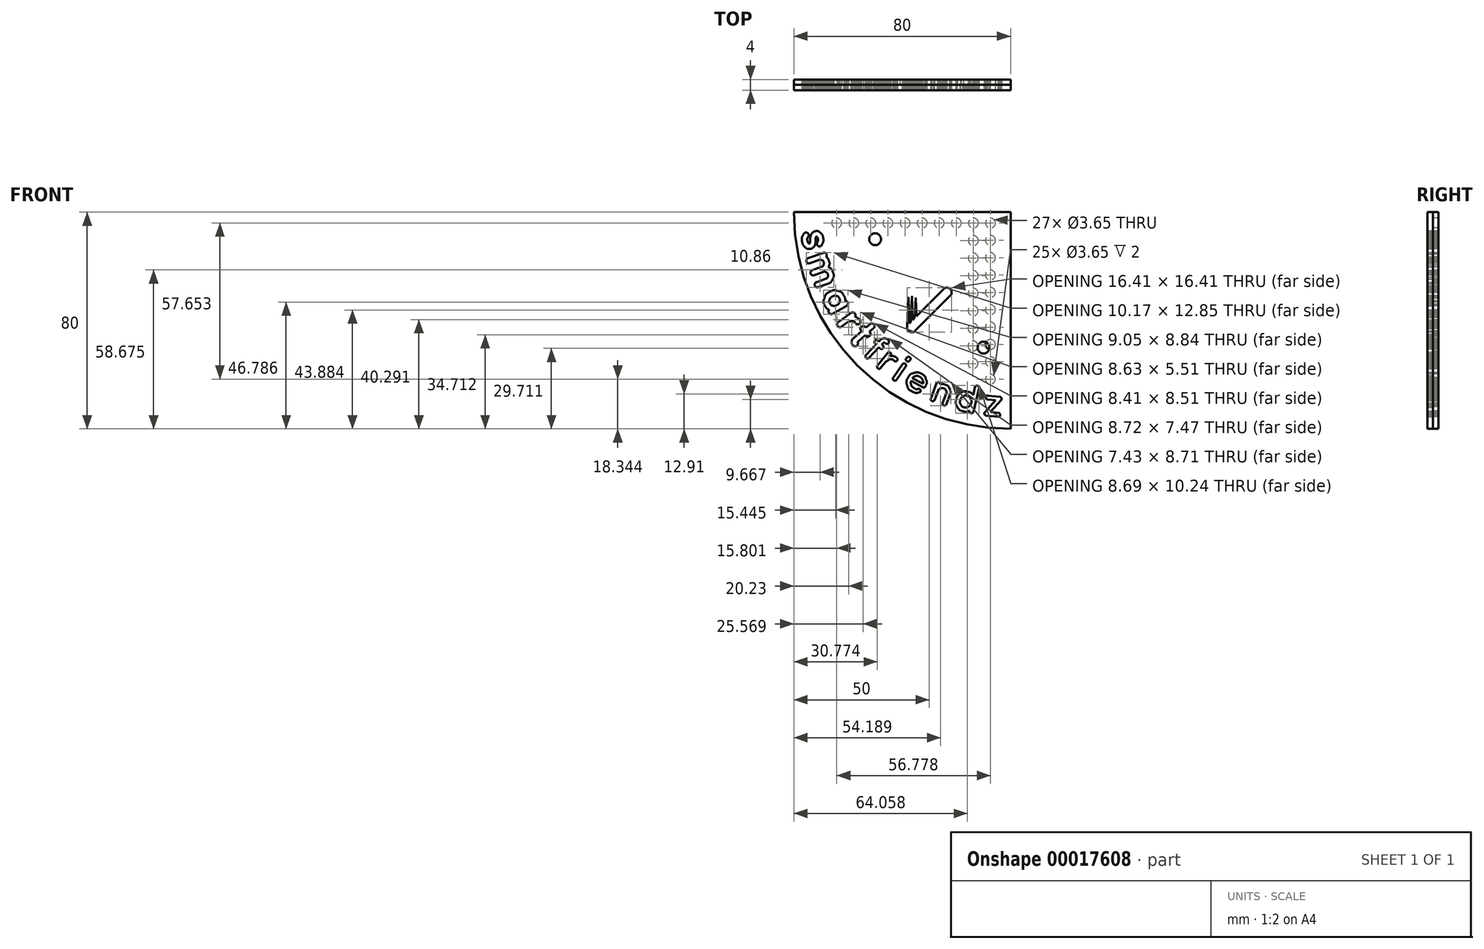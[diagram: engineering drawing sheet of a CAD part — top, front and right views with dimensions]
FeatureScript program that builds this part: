
annotation { "Feature Type Name" : "Feature", "Feature Type Description" : "" }
export const myFeature = defineFeature(function(context is Context, id is Id, definition is map)
    precondition{}
    {
        {
            var Q0;
            Q0=qCreatedBy(makeId("Front.planeOp"),FACE);
            var sketch = newSketch(context, id + "F0", { "sketchPlane" : qUnion([Q0])});
            skFitSpline(sketch, "E0", {"points": [v(17.73, 12.09) * mm, v(17.4, 12.41) * mm, v(16.98, 12.59) * mm, v(16.53, 12.59) * mm]});
            skFitSpline(sketch, "E1", {"points": [v(16.53, 12.59) * mm, v(16.05, 12.59) * mm, v(15.65, 12.41) * mm, v(15.33, 12.09) * mm]});
            skLineSegment(sketch, "E2", {"start": v(15.33, 12.09) * mm, "end": v(5.27, 2.03) * mm});
            skLineSegment(sketch, "E3", {"start": v(5.27, 2.03) * mm, "end": v(5.07, 8.86) * mm});
            skFitSpline(sketch, "E4", {"points": [v(5.07, 8.86) * mm, v(5.04, 8.88) * mm, v(5.02, 8.9) * mm, v(5, 8.93) * mm]});
            skLineSegment(sketch, "E5", {"start": v(5, 8.93) * mm, "end": v(4.72, 1.5) * mm});
            skLineSegment(sketch, "E6", {"start": v(4.72, 1.5) * mm, "end": v(3.94, 0.73) * mm});
            skLineSegment(sketch, "E7", {"start": v(3.94, 0.73) * mm, "end": v(3.67, 9.53) * mm});
            skLineSegment(sketch, "E8", {"start": v(3.67, 9.53) * mm, "end": v(3.64, 9.53) * mm});
            skLineSegment(sketch, "E9", {"start": v(3.64, 9.53) * mm, "end": v(3.32, 0.1) * mm});
            skLineSegment(sketch, "E10", {"start": v(3.32, 0.1) * mm, "end": v(2.64, -0.57) * mm});
            skLineSegment(sketch, "E11", {"start": v(2.64, -0.57) * mm, "end": v(2.37, 9) * mm});
            skFitSpline(sketch, "E12", {"points": [v(2.37, 9) * mm, v(2.35, 9) * mm, v(2.33, 8.97) * mm, v(2.32, 8.93) * mm]});
            skLineSegment(sketch, "E13", {"start": v(2.32, 8.93) * mm, "end": v(1.94, -1.57) * mm});
            skFitSpline(sketch, "E14", {"points": [v(1.94, -1.57) * mm, v(1.9, -1.72) * mm, v(1.87, -1.9) * mm, v(1.87, -2.07) * mm]});
            skFitSpline(sketch, "E15", {"points": [v(1.87, -2.07) * mm, v(1.87, -2.55) * mm, v(2.04, -2.95) * mm, v(2.37, -3.28) * mm]});
            skFitSpline(sketch, "E16", {"points": [v(2.37, -3.28) * mm, v(2.7, -3.6) * mm, v(3.12, -3.78) * mm, v(3.6, -3.8) * mm]});
            skFitSpline(sketch, "E17", {"points": [v(3.6, -3.8) * mm, v(4.07, -3.8) * mm, v(4.47, -3.65) * mm, v(4.82, -3.3) * mm]});
            skLineSegment(sketch, "E18", {"start": v(4.82, -3.3) * mm, "end": v(17.75, 9.63) * mm});
            skFitSpline(sketch, "E19", {"points": [v(17.75, 9.63) * mm, v(18.08, 9.98) * mm, v(18.25, 10.38) * mm, v(18.25, 10.86) * mm]});
            skFitSpline(sketch, "E20", {"points": [v(18.25, 10.86) * mm, v(18.23, 11.34) * mm, v(18.08, 11.76) * mm, v(17.73, 12.09) * mm]});
            skFitSpline(sketch, "E21", {"points": [v(9.35, 19.77) * mm, v(9.35, 20.24) * mm, v(9.17, 20.64) * mm, v(8.82, 21) * mm]});
            skFitSpline(sketch, "E22", {"points": [v(8.82, 21) * mm, v(8.5, 21.32) * mm, v(8.07, 21.5) * mm, v(7.62, 21.5) * mm]});
            skFitSpline(sketch, "E23", {"points": [v(7.62, 21.5) * mm, v(7.45, 21.5) * mm, v(7.3, 21.47) * mm, v(7.15, 21.42) * mm]});
            skLineSegment(sketch, "E24", {"start": v(7.15, 21.42) * mm, "end": v(-3.41, 21.1) * mm});
            skFitSpline(sketch, "E25", {"points": [v(-3.41, 21.1) * mm, v(-3.44, 21.07) * mm, v(-3.46, 21.07) * mm, v(-3.46, 21.04) * mm]});
            skLineSegment(sketch, "E26", {"start": v(-3.46, 21.04) * mm, "end": v(6.15, 20.7) * mm});
            skLineSegment(sketch, "E27", {"start": v(6.15, 20.7) * mm, "end": v(5.47, 20.02) * mm});
            skLineSegment(sketch, "E28", {"start": v(5.47, 20.02) * mm, "end": v(-4.09, 19.74) * mm});
            skLineSegment(sketch, "E29", {"start": v(-4.09, 19.74) * mm, "end": v(4.84, 19.42) * mm});
            skLineSegment(sketch, "E30", {"start": v(4.84, 19.42) * mm, "end": v(4.07, 18.64) * mm});
            skLineSegment(sketch, "E31", {"start": v(4.07, 18.64) * mm, "end": v(-3.56, 18.42) * mm});
            skFitSpline(sketch, "E32", {"points": [v(-3.56, 18.42) * mm, v(-3.54, 18.4) * mm, v(-3.54, 18.4) * mm, v(-3.51, 18.37) * mm]});
            skLineSegment(sketch, "E33", {"start": v(-3.51, 18.37) * mm, "end": v(3.57, 18.11) * mm});
            skLineSegment(sketch, "E34", {"start": v(3.57, 18.11) * mm, "end": v(-6.54, 8.06) * mm});
            skFitSpline(sketch, "E35", {"points": [v(-6.54, 8.06) * mm, v(-6.86, 7.73) * mm, v(-7.04, 7.3) * mm, v(-7.04, 6.86) * mm]});
            skFitSpline(sketch, "E36", {"points": [v(-7.04, 6.86) * mm, v(-7.04, 6.38) * mm, v(-6.86, 5.98) * mm, v(-6.54, 5.66) * mm]});
            skFitSpline(sketch, "E37", {"points": [v(-6.54, 5.66) * mm, v(-6.21, 5.33) * mm, v(-5.79, 5.16) * mm, v(-5.31, 5.13) * mm]});
            skFitSpline(sketch, "E38", {"points": [v(-5.31, 5.13) * mm, v(-4.84, 5.13) * mm, v(-4.44, 5.28) * mm, v(-4.09, 5.63) * mm]});
            skLineSegment(sketch, "E39", {"start": v(-4.09, 5.63) * mm, "end": v(8.85, 18.57) * mm});
            skFitSpline(sketch, "E40", {"points": [v(8.85, 18.57) * mm, v(9.2, 18.9) * mm, v(9.35, 19.3) * mm, v(9.35, 19.77) * mm]});
            skFitSpline(sketch, "E41", {"points": [v(-33.8, 26.97) * mm, v(-33.43, 27.05) * mm, v(-33.08, 27.22) * mm, v(-32.76, 27.52) * mm]});
            skFitSpline(sketch, "E42", {"points": [v(-32.76, 27.52) * mm, v(-32.43, 27.82) * mm, v(-32.18, 28.22) * mm, v(-32.06, 28.72) * mm]});
            skFitSpline(sketch, "E43", {"points": [v(-32.06, 28.72) * mm, v(-31.93, 29.2) * mm, v(-31.88, 29.7) * mm, v(-31.88, 30.25) * mm]});
            skLineSegment(sketch, "E44", {"start": v(-31.88, 30.25) * mm, "end": v(-31.88, 30.27) * mm});
            skLineSegment(sketch, "E45", {"start": v(-31.88, 30.27) * mm, "end": v(-31.88, 30.32) * mm});
            skFitSpline(sketch, "E46", {"points": [v(-31.88, 30.32) * mm, v(-31.88, 30.82) * mm, v(-31.83, 31.17) * mm, v(-31.73, 31.4) * mm]});
            skFitSpline(sketch, "E47", {"points": [v(-31.73, 31.4) * mm, v(-31.72, 31.45) * mm, v(-31.7, 31.48) * mm, v(-31.68, 31.5) * mm]});
            skFitSpline(sketch, "E48", {"points": [v(-31.68, 31.5) * mm, v(-31.66, 31.52) * mm, v(-31.64, 31.52) * mm, v(-31.6, 31.52) * mm]});
            skFitSpline(sketch, "E49", {"points": [v(-31.6, 31.52) * mm, v(-31.57, 31.52) * mm, v(-31.51, 31.47) * mm, v(-31.43, 31.37) * mm]});
            skFitSpline(sketch, "E50", {"points": [v(-31.43, 31.37) * mm, v(-31.26, 31.2) * mm, v(-31.13, 30.97) * mm, v(-31.06, 30.65) * mm]});
            skFitSpline(sketch, "E51", {"points": [v(-31.06, 30.65) * mm, v(-31, 30.32) * mm, v(-31.08, 29.87) * mm, v(-31.33, 29.3) * mm]});
            skFitSpline(sketch, "E52", {"points": [v(-31.33, 29.3) * mm, v(-31.46, 29.05) * mm, v(-31.46, 28.77) * mm, v(-31.36, 28.52) * mm]});
            skFitSpline(sketch, "E53", {"points": [v(-31.36, 28.52) * mm, v(-31.26, 28.27) * mm, v(-31.08, 28.1) * mm, v(-30.83, 27.97) * mm]});
            skFitSpline(sketch, "E54", {"points": [v(-30.83, 27.97) * mm, v(-30.58, 27.87) * mm, v(-30.33, 27.9) * mm, v(-30.08, 28) * mm]});
            skFitSpline(sketch, "E55", {"points": [v(-30.08, 28) * mm, v(-29.83, 28.1) * mm, v(-29.66, 28.27) * mm, v(-29.56, 28.52) * mm]});
            skFitSpline(sketch, "E56", {"points": [v(-29.56, 28.52) * mm, v(-29.15, 29.45) * mm, v(-29, 30.27) * mm, v(-29.13, 31) * mm]});
            skFitSpline(sketch, "E57", {"points": [v(-29.13, 31) * mm, v(-29.25, 31.72) * mm, v(-29.58, 32.33) * mm, v(-30.08, 32.83) * mm]});
            skFitSpline(sketch, "E58", {"points": [v(-30.08, 32.83) * mm, v(-30.68, 33.35) * mm, v(-31.33, 33.58) * mm, v(-32.03, 33.45) * mm]});
            skFitSpline(sketch, "E59", {"points": [v(-32.03, 33.45) * mm, v(-32.4, 33.38) * mm, v(-32.73, 33.23) * mm, v(-33, 32.98) * mm]});
            skFitSpline(sketch, "E60", {"points": [v(-33, 32.98) * mm, v(-33.33, 32.65) * mm, v(-33.58, 32.25) * mm, v(-33.7, 31.8) * mm]});
            skFitSpline(sketch, "E61", {"points": [v(-33.7, 31.8) * mm, v(-33.83, 31.35) * mm, v(-33.88, 30.85) * mm, v(-33.88, 30.3) * mm]});
            skLineSegment(sketch, "E62", {"start": v(-33.88, 30.3) * mm, "end": v(-33.88, 30.27) * mm});
            skFitSpline(sketch, "E63", {"points": [v(-33.88, 30.27) * mm, v(-33.88, 29.75) * mm, v(-33.96, 29.35) * mm, v(-34.06, 29.1) * mm]});
            skFitSpline(sketch, "E64", {"points": [v(-34.06, 29.1) * mm, v(-34.1, 29.03) * mm, v(-34.12, 28.99) * mm, v(-34.13, 28.97) * mm]});
            skLineSegment(sketch, "E65", {"start": v(-34.13, 28.97) * mm, "end": v(-34.16, 28.95) * mm});
            skFitSpline(sketch, "E66", {"points": [v(-34.16, 28.95) * mm, v(-34.18, 28.93) * mm, v(-34.2, 28.92) * mm, v(-34.26, 28.92) * mm]});
            skFitSpline(sketch, "E67", {"points": [v(-34.26, 28.92) * mm, v(-34.3, 28.92) * mm, v(-34.4, 28.97) * mm, v(-34.5, 29.07) * mm]});
            skFitSpline(sketch, "E68", {"points": [v(-34.5, 29.07) * mm, v(-34.73, 29.3) * mm, v(-34.86, 29.6) * mm, v(-34.93, 29.92) * mm]});
            skFitSpline(sketch, "E69", {"points": [v(-34.93, 29.92) * mm, v(-35.03, 30.42) * mm, v(-34.93, 30.97) * mm, v(-34.6, 31.52) * mm]});
            skFitSpline(sketch, "E70", {"points": [v(-34.6, 31.52) * mm, v(-34.48, 31.75) * mm, v(-34.43, 32) * mm, v(-34.5, 32.28) * mm]});
            skFitSpline(sketch, "E71", {"points": [v(-34.5, 32.28) * mm, v(-34.58, 32.55) * mm, v(-34.76, 32.75) * mm, v(-34.98, 32.85) * mm]});
            skFitSpline(sketch, "E72", {"points": [v(-34.98, 32.85) * mm, v(-35.2, 32.98) * mm, v(-35.46, 33.03) * mm, v(-35.73, 32.93) * mm]});
            skFitSpline(sketch, "E73", {"points": [v(-35.73, 32.93) * mm, v(-36, 32.85) * mm, v(-36.18, 32.7) * mm, v(-36.3, 32.48) * mm]});
            skFitSpline(sketch, "E74", {"points": [v(-36.3, 32.48) * mm, v(-36.84, 31.47) * mm, v(-37.04, 30.5) * mm, v(-36.86, 29.55) * mm]});
            skFitSpline(sketch, "E75", {"points": [v(-36.86, 29.55) * mm, v(-36.71, 28.8) * mm, v(-36.39, 28.17) * mm, v(-35.86, 27.65) * mm]});
            skFitSpline(sketch, "E76", {"points": [v(-35.86, 27.65) * mm, v(-35.36, 27.17) * mm, v(-34.83, 26.95) * mm, v(-34.23, 26.95) * mm]});
            skFitSpline(sketch, "E77", {"points": [v(-34.23, 26.95) * mm, v(-34.08, 26.92) * mm, v(-33.93, 26.95) * mm, v(-33.8, 26.97) * mm]});
            skFitSpline(sketch, "E78", {"points": [v(-25.65, 15.74) * mm, v(-25.25, 16.56) * mm, v(-25.23, 17.44) * mm, v(-25.55, 18.37) * mm]});
            skFitSpline(sketch, "E79", {"points": [v(-25.55, 18.37) * mm, v(-25.85, 19.22) * mm, v(-26.4, 19.82) * mm, v(-27.2, 20.2) * mm]});
            skFitSpline(sketch, "E80", {"points": [v(-27.2, 20.2) * mm, v(-26.83, 21) * mm, v(-26.78, 21.84) * mm, v(-27.1, 22.72) * mm]});
            skFitSpline(sketch, "E81", {"points": [v(-27.1, 22.72) * mm, v(-27.28, 23.22) * mm, v(-27.58, 23.67) * mm, v(-27.98, 24.04) * mm]});
            skFitSpline(sketch, "E82", {"points": [v(-27.98, 24.04) * mm, v(-27.8, 24.3) * mm, v(-27.78, 24.6) * mm, v(-27.88, 24.92) * mm]});
            skFitSpline(sketch, "E83", {"points": [v(-27.88, 24.92) * mm, v(-27.98, 25.17) * mm, v(-28.13, 25.37) * mm, v(-28.38, 25.47) * mm]});
            skFitSpline(sketch, "E84", {"points": [v(-28.38, 25.47) * mm, v(-28.63, 25.6) * mm, v(-28.88, 25.6) * mm, v(-29.15, 25.5) * mm]});
            skLineSegment(sketch, "E85", {"start": v(-29.15, 25.5) * mm, "end": v(-34.7, 23.52) * mm});
            skFitSpline(sketch, "E86", {"points": [v(-34.7, 23.52) * mm, v(-34.93, 23.44) * mm, v(-35.1, 23.3) * mm, v(-35.2, 23.1) * mm]});
            skFitSpline(sketch, "E87", {"points": [v(-35.2, 23.1) * mm, v(-35.3, 22.9) * mm, v(-35.36, 22.7) * mm, v(-35.33, 22.44) * mm]});
            skLineSegment(sketch, "E88", {"start": v(-35.33, 22.44) * mm, "end": v(-35.28, 22.27) * mm});
            skLineSegment(sketch, "E89", {"start": v(-35.28, 22.27) * mm, "end": v(-35.28, 22.24) * mm});
            skFitSpline(sketch, "E90", {"points": [v(-35.28, 22.24) * mm, v(-35.16, 21.87) * mm, v(-34.86, 21.62) * mm, v(-34.43, 21.57) * mm]});
            skLineSegment(sketch, "E91", {"start": v(-34.43, 21.57) * mm, "end": v(-34.38, 21.57) * mm});
            skLineSegment(sketch, "E92", {"start": v(-34.38, 21.57) * mm, "end": v(-34.3, 21.6) * mm});
            skLineSegment(sketch, "E93", {"start": v(-34.3, 21.6) * mm, "end": v(-34.2, 21.6) * mm});
            skLineSegment(sketch, "E94", {"start": v(-34.2, 21.6) * mm, "end": v(-34.06, 21.64) * mm});
            skLineSegment(sketch, "E95", {"start": v(-34.06, 21.64) * mm, "end": v(-30.68, 22.84) * mm});
            skFitSpline(sketch, "E96", {"points": [v(-30.68, 22.84) * mm, v(-30.33, 22.97) * mm, v(-29.98, 22.94) * mm, v(-29.63, 22.8) * mm]});
            skFitSpline(sketch, "E97", {"points": [v(-29.63, 22.8) * mm, v(-29.28, 22.64) * mm, v(-29.05, 22.4) * mm, v(-28.95, 22.04) * mm]});
            skFitSpline(sketch, "E98", {"points": [v(-28.95, 22.04) * mm, v(-28.83, 21.7) * mm, v(-28.85, 21.37) * mm, v(-29, 21.02) * mm]});
            skFitSpline(sketch, "E99", {"points": [v(-29, 21.02) * mm, v(-29.15, 20.67) * mm, v(-29.4, 20.44) * mm, v(-29.73, 20.32) * mm]});
            skLineSegment(sketch, "E100", {"start": v(-29.73, 20.32) * mm, "end": v(-33.13, 19.12) * mm});
            skFitSpline(sketch, "E101", {"points": [v(-33.13, 19.12) * mm, v(-33.38, 19.04) * mm, v(-33.56, 18.87) * mm, v(-33.68, 18.6) * mm]});
            skFitSpline(sketch, "E102", {"points": [v(-33.68, 18.6) * mm, v(-33.8, 18.34) * mm, v(-33.8, 18.09) * mm, v(-33.73, 17.84) * mm]});
            skFitSpline(sketch, "E103", {"points": [v(-33.73, 17.84) * mm, v(-33.63, 17.59) * mm, v(-33.48, 17.41) * mm, v(-33.23, 17.29) * mm]});
            skFitSpline(sketch, "E104", {"points": [v(-33.23, 17.29) * mm, v(-32.98, 17.16) * mm, v(-32.73, 17.16) * mm, v(-32.48, 17.24) * mm]});
            skLineSegment(sketch, "E105", {"start": v(-32.48, 17.24) * mm, "end": v(-29.1, 18.44) * mm});
            skFitSpline(sketch, "E106", {"points": [v(-29.1, 18.44) * mm, v(-28.75, 18.54) * mm, v(-28.4, 18.52) * mm, v(-28.08, 18.37) * mm]});
            skFitSpline(sketch, "E107", {"points": [v(-28.08, 18.37) * mm, v(-27.75, 18.2) * mm, v(-27.53, 17.94) * mm, v(-27.4, 17.61) * mm]});
            skFitSpline(sketch, "E108", {"points": [v(-27.4, 17.61) * mm, v(-27.28, 17.26) * mm, v(-27.3, 16.94) * mm, v(-27.45, 16.59) * mm]});
            skFitSpline(sketch, "E109", {"points": [v(-27.45, 16.59) * mm, v(-27.6, 16.24) * mm, v(-27.88, 16.01) * mm, v(-28.23, 15.89) * mm]});
            skLineSegment(sketch, "E110", {"start": v(-28.23, 15.89) * mm, "end": v(-31.58, 14.69) * mm});
            skFitSpline(sketch, "E111", {"points": [v(-31.58, 14.69) * mm, v(-31.83, 14.59) * mm, v(-32.03, 14.41) * mm, v(-32.13, 14.16) * mm]});
            skFitSpline(sketch, "E112", {"points": [v(-32.13, 14.16) * mm, v(-32.26, 13.91) * mm, v(-32.26, 13.66) * mm, v(-32.16, 13.41) * mm]});
            skFitSpline(sketch, "E113", {"points": [v(-32.16, 13.41) * mm, v(-32.06, 13.16) * mm, v(-31.9, 12.96) * mm, v(-31.66, 12.86) * mm]});
            skFitSpline(sketch, "E114", {"points": [v(-31.66, 12.86) * mm, v(-31.53, 12.79) * mm, v(-31.38, 12.76) * mm, v(-31.23, 12.76) * mm]});
            skFitSpline(sketch, "E115", {"points": [v(-31.23, 12.76) * mm, v(-31.13, 12.76) * mm, v(-31, 12.79) * mm, v(-30.9, 12.81) * mm]});
            skLineSegment(sketch, "E116", {"start": v(-30.9, 12.81) * mm, "end": v(-27.55, 14.01) * mm});
            skFitSpline(sketch, "E117", {"points": [v(-27.55, 14.01) * mm, v(-26.68, 14.34) * mm, v(-26.05, 14.91) * mm, v(-25.65, 15.74) * mm]});
            skFitSpline(sketch, "E118", {"points": [v(-20.05, 6.53) * mm, v(-19.97, 6.8) * mm, v(-20, 7.03) * mm, v(-20.12, 7.26) * mm]});
            skFitSpline(sketch, "E119", {"points": [v(-20.12, 7.26) * mm, v(-20.25, 7.48) * mm, v(-20.42, 7.63) * mm, v(-20.65, 7.7) * mm]});
            skFitSpline(sketch, "E120", {"points": [v(-20.65, 7.7) * mm, v(-20.77, 7.76) * mm, v(-20.92, 7.78) * mm, v(-21.05, 7.76) * mm]});
            skFitSpline(sketch, "E121", {"points": [v(-21.05, 7.76) * mm, v(-21.02, 8.46) * mm, v(-21.15, 9.1) * mm, v(-21.5, 9.68) * mm]});
            skFitSpline(sketch, "E122", {"points": [v(-21.5, 9.68) * mm, v(-22.02, 10.6) * mm, v(-22.8, 11.21) * mm, v(-23.83, 11.46) * mm]});
            skFitSpline(sketch, "E123", {"points": [v(-23.83, 11.46) * mm, v(-24.85, 11.71) * mm, v(-25.85, 11.56) * mm, v(-26.78, 11.03) * mm]});
            skFitSpline(sketch, "E124", {"points": [v(-26.78, 11.03) * mm, v(-27.73, 10.5) * mm, v(-28.35, 9.73) * mm, v(-28.68, 8.73) * mm]});
            skFitSpline(sketch, "E125", {"points": [v(-28.68, 8.73) * mm, v(-29, 7.73) * mm, v(-28.9, 6.76) * mm, v(-28.38, 5.83) * mm]});
            skFitSpline(sketch, "E126", {"points": [v(-28.38, 5.83) * mm, v(-28.05, 5.23) * mm, v(-27.58, 4.78) * mm, v(-26.98, 4.43) * mm]});
            skFitSpline(sketch, "E127", {"points": [v(-26.98, 4.43) * mm, v(-27.05, 4.3) * mm, v(-27.1, 4.18) * mm, v(-27.13, 4.05) * mm]});
            skFitSpline(sketch, "E128", {"points": [v(-27.13, 4.05) * mm, v(-27.18, 3.83) * mm, v(-27.13, 3.6) * mm, v(-27, 3.38) * mm]});
            skFitSpline(sketch, "E129", {"points": [v(-27, 3.38) * mm, v(-26.88, 3.15) * mm, v(-26.68, 3) * mm, v(-26.43, 2.93) * mm]});
            skFitSpline(sketch, "E130", {"points": [v(-26.43, 2.93) * mm, v(-26.33, 2.9) * mm, v(-26.25, 2.88) * mm, v(-26.15, 2.88) * mm]});
            skFitSpline(sketch, "E131", {"points": [v(-26.15, 2.88) * mm, v(-26, 2.88) * mm, v(-25.83, 2.93) * mm, v(-25.68, 3) * mm]});
            skLineSegment(sketch, "E132", {"start": v(-25.68, 3) * mm, "end": v(-20.52, 5.88) * mm});
            skFitSpline(sketch, "E133", {"points": [v(-20.52, 5.88) * mm, v(-20.27, 6.08) * mm, v(-20.12, 6.28) * mm, v(-20.05, 6.53) * mm]});
            skFitSpline(sketch, "E134", {"points": [v(-23.1, 7.36) * mm, v(-23.28, 6.86) * mm, v(-23.58, 6.48) * mm, v(-24.08, 6.2) * mm]});
            skFitSpline(sketch, "E135", {"points": [v(-24.08, 6.2) * mm, v(-24.55, 5.93) * mm, v(-25.05, 5.86) * mm, v(-25.53, 5.98) * mm]});
            skFitSpline(sketch, "E136", {"points": [v(-25.53, 5.98) * mm, v(-26.03, 6.1) * mm, v(-26.38, 6.38) * mm, v(-26.63, 6.83) * mm]});
            skFitSpline(sketch, "E137", {"points": [v(-26.63, 6.83) * mm, v(-26.88, 7.28) * mm, v(-26.93, 7.73) * mm, v(-26.75, 8.2) * mm]});
            skFitSpline(sketch, "E138", {"points": [v(-26.75, 8.2) * mm, v(-26.58, 8.68) * mm, v(-26.28, 9.06) * mm, v(-25.78, 9.33) * mm]});
            skFitSpline(sketch, "E139", {"points": [v(-25.78, 9.33) * mm, v(-25.43, 9.53) * mm, v(-25.08, 9.63) * mm, v(-24.73, 9.63) * mm]});
            skFitSpline(sketch, "E140", {"points": [v(-24.73, 9.63) * mm, v(-24.58, 9.63) * mm, v(-24.43, 9.6) * mm, v(-24.3, 9.58) * mm]});
            skFitSpline(sketch, "E141", {"points": [v(-24.3, 9.58) * mm, v(-23.8, 9.48) * mm, v(-23.45, 9.2) * mm, v(-23.2, 8.76) * mm]});
            skFitSpline(sketch, "E142", {"points": [v(-23.2, 8.76) * mm, v(-22.98, 8.3) * mm, v(-22.93, 7.86) * mm, v(-23.1, 7.36) * mm]});
            skFitSpline(sketch, "E143", {"points": [v(-17.2, -0.47) * mm, v(-17.05, -0.7) * mm, v(-16.82, -0.82) * mm, v(-16.55, -0.87) * mm]});
            skFitSpline(sketch, "E144", {"points": [v(-16.55, -0.87) * mm, v(-16.27, -0.92) * mm, v(-16.02, -0.85) * mm, v(-15.82, -0.7) * mm]});
            skFitSpline(sketch, "E145", {"points": [v(-15.82, -0.7) * mm, v(-15.6, -0.55) * mm, v(-15.47, -0.32) * mm, v(-15.45, -0.07) * mm]});
            skFitSpline(sketch, "E146", {"points": [v(-15.45, -0.07) * mm, v(-15.4, 0.18) * mm, v(-15.5, 0.48) * mm, v(-15.72, 0.78) * mm]});
            skFitSpline(sketch, "E147", {"points": [v(-15.72, 0.78) * mm, v(-15.92, 1.08) * mm, v(-16.22, 1.33) * mm, v(-16.62, 1.58) * mm]});
            skFitSpline(sketch, "E148", {"points": [v(-16.62, 1.58) * mm, v(-16.87, 1.73) * mm, v(-17.15, 1.85) * mm, v(-17.4, 1.93) * mm]});
            skFitSpline(sketch, "E149", {"points": [v(-17.4, 1.93) * mm, v(-17.3, 2.05) * mm, v(-17.25, 2.2) * mm, v(-17.22, 2.38) * mm]});
            skFitSpline(sketch, "E150", {"points": [v(-17.22, 2.38) * mm, v(-17.2, 2.65) * mm, v(-17.25, 2.88) * mm, v(-17.42, 3.1) * mm]});
            skFitSpline(sketch, "E151", {"points": [v(-17.42, 3.1) * mm, v(-17.57, 3.33) * mm, v(-17.8, 3.45) * mm, v(-18.05, 3.5) * mm]});
            skFitSpline(sketch, "E152", {"points": [v(-18.05, 3.5) * mm, v(-18.32, 3.55) * mm, v(-18.55, 3.5) * mm, v(-18.77, 3.33) * mm]});
            skLineSegment(sketch, "E153", {"start": v(-18.77, 3.33) * mm, "end": v(-23.58, -0.12) * mm});
            skFitSpline(sketch, "E154", {"points": [v(-23.58, -0.12) * mm, v(-23.8, -0.27) * mm, v(-23.93, -0.5) * mm, v(-23.98, -0.77) * mm]});
            skFitSpline(sketch, "E155", {"points": [v(-23.98, -0.77) * mm, v(-24.03, -1.05) * mm, v(-23.95, -1.3) * mm, v(-23.8, -1.52) * mm]});
            skFitSpline(sketch, "E156", {"points": [v(-23.8, -1.52) * mm, v(-23.65, -1.75) * mm, v(-23.43, -1.87) * mm, v(-23.15, -1.92) * mm]});
            skFitSpline(sketch, "E157", {"points": [v(-23.15, -1.92) * mm, v(-23.1, -1.92) * mm, v(-23.03, -1.95) * mm, v(-22.98, -1.95) * mm]});
            skFitSpline(sketch, "E158", {"points": [v(-22.98, -1.95) * mm, v(-22.78, -1.95) * mm, v(-22.6, -1.9) * mm, v(-22.43, -1.77) * mm]});
            skLineSegment(sketch, "E159", {"start": v(-22.43, -1.77) * mm, "end": v(-20.15, -0.12) * mm});
            skFitSpline(sketch, "E160", {"points": [v(-20.15, -0.12) * mm, v(-18.67, 0.33) * mm, v(-17.7, 0.2) * mm, v(-17.2, -0.47) * mm]});
            skFitSpline(sketch, "E161", {"points": [v(-10.2, -1.62) * mm, v(-10.17, -1.35) * mm, v(-10.27, -1.1) * mm, v(-10.44, -0.9) * mm]});
            skFitSpline(sketch, "E162", {"points": [v(-10.44, -0.9) * mm, v(-10.62, -0.7) * mm, v(-10.87, -0.57) * mm, v(-11.14, -0.55) * mm]});
            skFitSpline(sketch, "E163", {"points": [v(-11.14, -0.55) * mm, v(-11.42, -0.52) * mm, v(-11.67, -0.6) * mm, v(-11.9, -0.8) * mm]});
            skLineSegment(sketch, "E164", {"start": v(-11.9, -0.8) * mm, "end": v(-13.4, -2.1) * mm});
            skLineSegment(sketch, "E165", {"start": v(-13.4, -2.1) * mm, "end": v(-13.57, -1.92) * mm});
            skFitSpline(sketch, "E166", {"points": [v(-13.57, -1.92) * mm, v(-13.74, -1.72) * mm, v(-14, -1.6) * mm, v(-14.27, -1.57) * mm]});
            skFitSpline(sketch, "E167", {"points": [v(-14.27, -1.57) * mm, v(-14.54, -1.55) * mm, v(-14.8, -1.65) * mm, v(-15, -1.82) * mm]});
            skFitSpline(sketch, "E168", {"points": [v(-15, -1.82) * mm, v(-15.2, -2) * mm, v(-15.32, -2.25) * mm, v(-15.35, -2.52) * mm]});
            skFitSpline(sketch, "E169", {"points": [v(-15.35, -2.52) * mm, v(-15.37, -2.8) * mm, v(-15.27, -3.05) * mm, v(-15.1, -3.25) * mm]});
            skLineSegment(sketch, "E170", {"start": v(-15.1, -3.25) * mm, "end": v(-14.92, -3.43) * mm});
            skLineSegment(sketch, "E171", {"start": v(-14.92, -3.43) * mm, "end": v(-17.92, -6.05) * mm});
            skFitSpline(sketch, "E172", {"points": [v(-17.92, -6.05) * mm, v(-18.3, -6.38) * mm, v(-18.52, -6.83) * mm, v(-18.55, -7.33) * mm]});
            skFitSpline(sketch, "E173", {"points": [v(-18.55, -7.33) * mm, v(-18.57, -7.83) * mm, v(-18.42, -8.28) * mm, v(-18.1, -8.68) * mm]});
            skFitSpline(sketch, "E174", {"points": [v(-18.1, -8.68) * mm, v(-17.92, -8.88) * mm, v(-17.67, -9) * mm, v(-17.4, -9.03) * mm]});
            skFitSpline(sketch, "E175", {"points": [v(-17.4, -9.03) * mm, v(-17.37, -9.03) * mm, v(-17.35, -9.03) * mm, v(-17.32, -9.03) * mm]});
            skFitSpline(sketch, "E176", {"points": [v(-17.32, -9.03) * mm, v(-17.07, -9.03) * mm, v(-16.85, -8.95) * mm, v(-16.67, -8.78) * mm]});
            skFitSpline(sketch, "E177", {"points": [v(-16.67, -8.78) * mm, v(-16.47, -8.6) * mm, v(-16.35, -8.35) * mm, v(-16.32, -8.08) * mm]});
            skFitSpline(sketch, "E178", {"points": [v(-16.32, -8.08) * mm, v(-16.3, -7.85) * mm, v(-16.35, -7.65) * mm, v(-16.45, -7.48) * mm]});
            skLineSegment(sketch, "E179", {"start": v(-16.45, -7.48) * mm, "end": v(-13.57, -4.95) * mm});
            skLineSegment(sketch, "E180", {"start": v(-13.57, -4.95) * mm, "end": v(-13.44, -5.1) * mm});
            skFitSpline(sketch, "E181", {"points": [v(-13.44, -5.1) * mm, v(-13.27, -5.3) * mm, v(-13.02, -5.43) * mm, v(-12.74, -5.45) * mm]});
            skFitSpline(sketch, "E182", {"points": [v(-12.74, -5.45) * mm, v(-12.47, -5.48) * mm, v(-12.22, -5.38) * mm, v(-12, -5.2) * mm]});
            skFitSpline(sketch, "E183", {"points": [v(-12, -5.2) * mm, v(-11.8, -5.03) * mm, v(-11.67, -4.78) * mm, v(-11.67, -4.5) * mm]});
            skFitSpline(sketch, "E184", {"points": [v(-11.67, -4.5) * mm, v(-11.64, -4.23) * mm, v(-11.74, -3.98) * mm, v(-11.92, -3.78) * mm]});
            skLineSegment(sketch, "E185", {"start": v(-11.92, -3.78) * mm, "end": v(-12.04, -3.63) * mm});
            skLineSegment(sketch, "E186", {"start": v(-12.04, -3.63) * mm, "end": v(-10.54, -2.32) * mm});
            skFitSpline(sketch, "E187", {"points": [v(-10.54, -2.32) * mm, v(-10.32, -2.15) * mm, v(-10.2, -1.9) * mm, v(-10.2, -1.62) * mm]});
            skFitSpline(sketch, "E188", {"points": [v(-4.81, -7.33) * mm, v(-4.81, -7.1) * mm, v(-4.89, -6.93) * mm, v(-5.04, -6.8) * mm]});
            skFitSpline(sketch, "E189", {"points": [v(-5.04, -6.8) * mm, v(-5.56, -6.3) * mm, v(-6.11, -6.05) * mm, v(-6.66, -6.1) * mm]});
            skFitSpline(sketch, "E190", {"points": [v(-6.66, -6.1) * mm, v(-7.21, -6.15) * mm, v(-7.76, -6.45) * mm, v(-8.34, -7.05) * mm]});
            skLineSegment(sketch, "E191", {"start": v(-8.34, -7.05) * mm, "end": v(-8.54, -7.25) * mm});
            skLineSegment(sketch, "E192", {"start": v(-8.54, -7.25) * mm, "end": v(-8.87, -6.93) * mm});
            skFitSpline(sketch, "E193", {"points": [v(-8.87, -6.93) * mm, v(-9.02, -6.78) * mm, v(-9.2, -6.7) * mm, v(-9.42, -6.7) * mm]});
            skFitSpline(sketch, "E194", {"points": [v(-9.42, -6.7) * mm, v(-9.64, -6.7) * mm, v(-9.82, -6.78) * mm, v(-9.97, -6.93) * mm]});
            skFitSpline(sketch, "E195", {"points": [v(-9.97, -6.93) * mm, v(-10.12, -7.08) * mm, v(-10.2, -7.25) * mm, v(-10.17, -7.48) * mm]});
            skFitSpline(sketch, "E196", {"points": [v(-10.17, -7.48) * mm, v(-10.17, -7.7) * mm, v(-10.1, -7.88) * mm, v(-9.92, -8.03) * mm]});
            skLineSegment(sketch, "E197", {"start": v(-9.92, -8.03) * mm, "end": v(-9.6, -8.35) * mm});
            skLineSegment(sketch, "E198", {"start": v(-9.6, -8.35) * mm, "end": v(-9.64, -8.4) * mm});
            skLineSegment(sketch, "E199", {"start": v(-9.64, -8.4) * mm, "end": v(-13.3, -12.2) * mm});
            skFitSpline(sketch, "E200", {"points": [v(-13.3, -12.2) * mm, v(-13.44, -12.36) * mm, v(-13.52, -12.53) * mm, v(-13.52, -12.76) * mm]});
            skFitSpline(sketch, "E201", {"points": [v(-13.52, -12.76) * mm, v(-13.52, -12.96) * mm, v(-13.44, -13.13) * mm, v(-13.3, -13.28) * mm]});
            skFitSpline(sketch, "E202", {"points": [v(-13.3, -13.28) * mm, v(-13.14, -13.43) * mm, v(-12.97, -13.5) * mm, v(-12.74, -13.5) * mm]});
            skFitSpline(sketch, "E203", {"points": [v(-12.74, -13.5) * mm, v(-12.54, -13.5) * mm, v(-12.37, -13.43) * mm, v(-12.22, -13.28) * mm]});
            skLineSegment(sketch, "E204", {"start": v(-12.22, -13.28) * mm, "end": v(-8.52, -9.4) * mm});
            skLineSegment(sketch, "E205", {"start": v(-8.52, -9.4) * mm, "end": v(-8.14, -9.75) * mm});
            skFitSpline(sketch, "E206", {"points": [v(-8.14, -9.75) * mm, v(-7.99, -9.9) * mm, v(-7.81, -9.98) * mm, v(-7.59, -9.95) * mm]});
            skFitSpline(sketch, "E207", {"points": [v(-7.59, -9.95) * mm, v(-7.36, -9.95) * mm, v(-7.19, -9.88) * mm, v(-7.06, -9.73) * mm]});
            skFitSpline(sketch, "E208", {"points": [v(-7.06, -9.73) * mm, v(-6.91, -9.58) * mm, v(-6.84, -9.4) * mm, v(-6.86, -9.18) * mm]});
            skFitSpline(sketch, "E209", {"points": [v(-6.86, -9.18) * mm, v(-6.86, -8.98) * mm, v(-6.94, -8.8) * mm, v(-7.09, -8.65) * mm]});
            skLineSegment(sketch, "E210", {"start": v(-7.09, -8.65) * mm, "end": v(-7.46, -8.3) * mm});
            skLineSegment(sketch, "E211", {"start": v(-7.46, -8.3) * mm, "end": v(-7.26, -8.1) * mm});
            skFitSpline(sketch, "E212", {"points": [v(-7.26, -8.1) * mm, v(-7.14, -7.98) * mm, v(-7.01, -7.85) * mm, v(-6.89, -7.75) * mm]});
            skFitSpline(sketch, "E213", {"points": [v(-6.89, -7.75) * mm, v(-6.76, -7.65) * mm, v(-6.66, -7.58) * mm, v(-6.59, -7.63) * mm]});
            skFitSpline(sketch, "E214", {"points": [v(-6.59, -7.63) * mm, v(-6.49, -7.63) * mm, v(-6.36, -7.73) * mm, v(-6.16, -7.9) * mm]});
            skFitSpline(sketch, "E215", {"points": [v(-6.16, -7.9) * mm, v(-5.99, -8.05) * mm, v(-5.81, -8.13) * mm, v(-5.59, -8.13) * mm]});
            skFitSpline(sketch, "E216", {"points": [v(-5.59, -8.13) * mm, v(-5.36, -8.13) * mm, v(-5.19, -8.05) * mm, v(-5.06, -7.9) * mm]});
            skFitSpline(sketch, "E217", {"points": [v(-5.06, -7.9) * mm, v(-4.89, -7.73) * mm, v(-4.81, -7.55) * mm, v(-4.81, -7.33) * mm]});
            skFitSpline(sketch, "E218", {"points": [v(-2.36, -14.56) * mm, v(-2.16, -14.53) * mm, v(-1.99, -14.43) * mm, v(-1.86, -14.28) * mm]});
            skFitSpline(sketch, "E219", {"points": [v(-1.86, -14.28) * mm, v(-1.74, -14.13) * mm, v(-1.69, -13.96) * mm, v(-1.71, -13.76) * mm]});
            skFitSpline(sketch, "E220", {"points": [v(-1.71, -13.76) * mm, v(-1.74, -13.56) * mm, v(-1.86, -13.36) * mm, v(-2.11, -13.16) * mm]});
            skFitSpline(sketch, "E221", {"points": [v(-2.11, -13.16) * mm, v(-2.36, -12.96) * mm, v(-2.69, -12.78) * mm, v(-3.09, -12.68) * mm]});
            skFitSpline(sketch, "E222", {"points": [v(-3.09, -12.68) * mm, v(-3.49, -12.56) * mm, v(-3.86, -12.53) * mm, v(-4.21, -12.6) * mm]});
            skLineSegment(sketch, "E223", {"start": v(-4.21, -12.6) * mm, "end": v(-4.39, -12.63) * mm});
            skLineSegment(sketch, "E224", {"start": v(-4.39, -12.63) * mm, "end": v(-4.21, -12.4) * mm});
            skFitSpline(sketch, "E225", {"points": [v(-4.21, -12.4) * mm, v(-4.09, -12.26) * mm, v(-4.04, -12.08) * mm, v(-4.06, -11.88) * mm]});
            skFitSpline(sketch, "E226", {"points": [v(-4.06, -11.88) * mm, v(-4.09, -11.68) * mm, v(-4.19, -11.5) * mm, v(-4.34, -11.38) * mm]});
            skFitSpline(sketch, "E227", {"points": [v(-4.34, -11.38) * mm, v(-4.49, -11.26) * mm, v(-4.64, -11.2) * mm, v(-4.81, -11.2) * mm]});
            skFitSpline(sketch, "E228", {"points": [v(-4.81, -11.2) * mm, v(-4.83, -11.2) * mm, v(-4.85, -11.2) * mm, v(-4.89, -11.2) * mm]});
            skFitSpline(sketch, "E229", {"points": [v(-4.89, -11.2) * mm, v(-5.09, -11.23) * mm, v(-5.24, -11.3) * mm, v(-5.36, -11.48) * mm]});
            skLineSegment(sketch, "E230", {"start": v(-5.36, -11.48) * mm, "end": v(-9.07, -16.08) * mm});
            skFitSpline(sketch, "E231", {"points": [v(-9.07, -16.08) * mm, v(-9.2, -16.23) * mm, v(-9.24, -16.4) * mm, v(-9.22, -16.63) * mm]});
            skFitSpline(sketch, "E232", {"points": [v(-9.22, -16.63) * mm, v(-9.2, -16.83) * mm, v(-9.1, -17) * mm, v(-8.94, -17.14) * mm]});
            skFitSpline(sketch, "E233", {"points": [v(-8.94, -17.14) * mm, v(-8.77, -17.26) * mm, v(-8.6, -17.31) * mm, v(-8.4, -17.31) * mm]});
            skFitSpline(sketch, "E234", {"points": [v(-8.4, -17.31) * mm, v(-8.19, -17.29) * mm, v(-8.01, -17.21) * mm, v(-7.89, -17.04) * mm]});
            skLineSegment(sketch, "E235", {"start": v(-7.89, -17.04) * mm, "end": v(-6.09, -14.78) * mm});
            skFitSpline(sketch, "E236", {"points": [v(-6.09, -14.78) * mm, v(-4.71, -13.93) * mm, v(-3.61, -13.8) * mm, v(-2.89, -14.4) * mm]});
            skFitSpline(sketch, "E237", {"points": [v(-2.89, -14.4) * mm, v(-2.74, -14.53) * mm, v(-2.56, -14.58) * mm, v(-2.36, -14.56) * mm]});
            skFitSpline(sketch, "E238", {"points": [v(1.12, -15.48) * mm, v(1, -15.38) * mm, v(0.84, -15.36) * mm, v(0.7, -15.36) * mm]});
            skFitSpline(sketch, "E239", {"points": [v(0.7, -15.36) * mm, v(0.64, -15.36) * mm, v(0.6, -15.36) * mm, v(0.54, -15.38) * mm]});
            skFitSpline(sketch, "E240", {"points": [v(0.54, -15.38) * mm, v(0.34, -15.43) * mm, v(0.2, -15.53) * mm, v(0.07, -15.7) * mm]});
            skLineSegment(sketch, "E241", {"start": v(0.07, -15.7) * mm, "end": v(-3.24, -20.54) * mm});
            skFitSpline(sketch, "E242", {"points": [v(-3.24, -20.54) * mm, v(-3.36, -20.71) * mm, v(-3.39, -20.89) * mm, v(-3.36, -21.09) * mm]});
            skFitSpline(sketch, "E243", {"points": [v(-3.36, -21.09) * mm, v(-3.31, -21.29) * mm, v(-3.21, -21.46) * mm, v(-3.04, -21.56) * mm]});
            skFitSpline(sketch, "E244", {"points": [v(-3.04, -21.56) * mm, v(-2.86, -21.69) * mm, v(-2.69, -21.71) * mm, v(-2.49, -21.69) * mm]});
            skFitSpline(sketch, "E245", {"points": [v(-2.49, -21.69) * mm, v(-2.29, -21.64) * mm, v(-2.14, -21.54) * mm, v(-2.01, -21.36) * mm]});
            skLineSegment(sketch, "E246", {"start": v(-2.01, -21.36) * mm, "end": v(1.3, -16.53) * mm});
            skFitSpline(sketch, "E247", {"points": [v(1.3, -16.53) * mm, v(1.42, -16.36) * mm, v(1.47, -16.16) * mm, v(1.42, -15.96) * mm]});
            skFitSpline(sketch, "E248", {"points": [v(1.42, -15.96) * mm, v(1.4, -15.76) * mm, v(1.3, -15.58) * mm, v(1.12, -15.48) * mm]});
            skFitSpline(sketch, "E249", {"points": [v(2.34, -14.6) * mm, v(2.54, -14.56) * mm, v(2.7, -14.46) * mm, v(2.82, -14.28) * mm]});
            skLineSegment(sketch, "E250", {"start": v(2.82, -14.28) * mm, "end": v(3, -14.03) * mm});
            skFitSpline(sketch, "E251", {"points": [v(3, -14.03) * mm, v(3.12, -13.86) * mm, v(3.14, -13.68) * mm, v(3.12, -13.48) * mm]});
            skFitSpline(sketch, "E252", {"points": [v(3.12, -13.48) * mm, v(3.07, -13.28) * mm, v(2.97, -13.13) * mm, v(2.8, -13) * mm]});
            skFitSpline(sketch, "E253", {"points": [v(2.8, -13) * mm, v(2.67, -12.9) * mm, v(2.52, -12.88) * mm, v(2.37, -12.88) * mm]});
            skFitSpline(sketch, "E254", {"points": [v(2.37, -12.88) * mm, v(2.32, -12.88) * mm, v(2.27, -12.88) * mm, v(2.22, -12.9) * mm]});
            skFitSpline(sketch, "E255", {"points": [v(2.22, -12.9) * mm, v(2.02, -12.96) * mm, v(1.84, -13.06) * mm, v(1.74, -13.2) * mm]});
            skLineSegment(sketch, "E256", {"start": v(1.74, -13.2) * mm, "end": v(1.57, -13.46) * mm});
            skFitSpline(sketch, "E257", {"points": [v(1.57, -13.46) * mm, v(1.44, -13.63) * mm, v(1.42, -13.83) * mm, v(1.44, -14.03) * mm]});
            skFitSpline(sketch, "E258", {"points": [v(1.44, -14.03) * mm, v(1.5, -14.23) * mm, v(1.6, -14.4) * mm, v(1.77, -14.5) * mm]});
            skFitSpline(sketch, "E259", {"points": [v(1.77, -14.5) * mm, v(1.97, -14.6) * mm, v(2.14, -14.66) * mm, v(2.34, -14.6) * mm]});
            skFitSpline(sketch, "E260", {"points": [v(7.1, -19.11) * mm, v(6.57, -18.84) * mm, v(6.02, -18.69) * mm, v(5.47, -18.69) * mm]});
            skFitSpline(sketch, "E261", {"points": [v(5.47, -18.69) * mm, v(5.12, -18.69) * mm, v(4.74, -18.74) * mm, v(4.37, -18.86) * mm]});
            skFitSpline(sketch, "E262", {"points": [v(4.37, -18.86) * mm, v(3.42, -19.16) * mm, v(2.7, -19.76) * mm, v(2.2, -20.64) * mm]});
            skFitSpline(sketch, "E263", {"points": [v(2.2, -20.64) * mm, v(1.72, -21.54) * mm, v(1.62, -22.46) * mm, v(1.87, -23.41) * mm]});
            skFitSpline(sketch, "E264", {"points": [v(1.87, -23.41) * mm, v(2.14, -24.37) * mm, v(2.72, -25.12) * mm, v(3.62, -25.6) * mm]});
            skFitSpline(sketch, "E265", {"points": [v(3.62, -25.6) * mm, v(4.52, -26.1) * mm, v(5.44, -26.22) * mm, v(6.37, -26) * mm]});
            skFitSpline(sketch, "E266", {"points": [v(6.37, -26) * mm, v(6.75, -25.84) * mm, v(6.87, -25.6) * mm, v(6.8, -25.22) * mm]});
            skFitSpline(sketch, "E267", {"points": [v(6.8, -25.22) * mm, v(6.77, -25.07) * mm, v(6.67, -24.94) * mm, v(6.47, -24.84) * mm]});
            skFitSpline(sketch, "E268", {"points": [v(6.47, -24.84) * mm, v(6.27, -24.74) * mm, v(6.07, -24.72) * mm, v(5.87, -24.77) * mm]});
            skFitSpline(sketch, "E269", {"points": [v(5.87, -24.77) * mm, v(5.3, -24.84) * mm, v(4.74, -24.7) * mm, v(4.24, -24.32) * mm]});
            skFitSpline(sketch, "E270", {"points": [v(4.24, -24.32) * mm, v(3.72, -23.94) * mm, v(3.42, -23.51) * mm, v(3.32, -23.01) * mm]});
            skFitSpline(sketch, "E271", {"points": [v(3.32, -23.01) * mm, v(3.22, -22.69) * mm, v(3.22, -22.29) * mm, v(3.34, -21.86) * mm]});
            skLineSegment(sketch, "E272", {"start": v(3.34, -21.86) * mm, "end": v(3.37, -21.79) * mm});
            skLineSegment(sketch, "E273", {"start": v(3.37, -21.79) * mm, "end": v(7.62, -24.12) * mm});
            skFitSpline(sketch, "E274", {"points": [v(7.62, -24.12) * mm, v(7.82, -24.22) * mm, v(8, -24.27) * mm, v(8.17, -24.22) * mm]});
            skFitSpline(sketch, "E275", {"points": [v(8.17, -24.22) * mm, v(8.35, -24.17) * mm, v(8.47, -24.06) * mm, v(8.57, -23.89) * mm]});
            skLineSegment(sketch, "E276", {"start": v(8.57, -23.89) * mm, "end": v(8.6, -23.81) * mm});
            skFitSpline(sketch, "E277", {"points": [v(8.6, -23.81) * mm, v(9.02, -22.91) * mm, v(9.1, -22.01) * mm, v(8.8, -21.14) * mm]});
            skFitSpline(sketch, "E278", {"points": [v(8.8, -21.14) * mm, v(8.52, -20.26) * mm, v(7.95, -19.59) * mm, v(7.1, -19.11) * mm]});
            skLineSegment(sketch, "E279", {"start": v(7.72, -22.79) * mm, "end": v(7.7, -22.86) * mm});
            skLineSegment(sketch, "E280", {"start": v(7.7, -22.86) * mm, "end": v(3.82, -20.76) * mm});
            skLineSegment(sketch, "E281", {"start": v(3.82, -20.76) * mm, "end": v(3.87, -20.71) * mm});
            skFitSpline(sketch, "E282", {"points": [v(3.87, -20.71) * mm, v(4.12, -20.41) * mm, v(4.47, -20.19) * mm, v(4.97, -20.06) * mm]});
            skFitSpline(sketch, "E283", {"points": [v(4.97, -20.06) * mm, v(5.44, -19.94) * mm, v(5.97, -20.01) * mm, v(6.5, -20.26) * mm]});
            skFitSpline(sketch, "E284", {"points": [v(6.5, -20.26) * mm, v(7, -20.59) * mm, v(7.37, -21.01) * mm, v(7.55, -21.51) * mm]});
            skFitSpline(sketch, "E285", {"points": [v(7.55, -21.51) * mm, v(7.77, -22.01) * mm, v(7.82, -22.44) * mm, v(7.72, -22.79) * mm]});
            skFitSpline(sketch, "E286", {"points": [v(15.83, -23.14) * mm, v(15.3, -22.94) * mm, v(14.75, -22.89) * mm, v(14.2, -23.01) * mm]});
            skLineSegment(sketch, "E287", {"start": v(14.2, -23.01) * mm, "end": v(14.13, -23.04) * mm});
            skLineSegment(sketch, "E288", {"start": v(14.13, -23.04) * mm, "end": v(14.13, -22.96) * mm});
            skFitSpline(sketch, "E289", {"points": [v(14.13, -22.96) * mm, v(14.1, -22.64) * mm, v(13.95, -22.44) * mm, v(13.65, -22.31) * mm]});
            skFitSpline(sketch, "E290", {"points": [v(13.65, -22.31) * mm, v(13.45, -22.24) * mm, v(13.28, -22.24) * mm, v(13.1, -22.34) * mm]});
            skFitSpline(sketch, "E291", {"points": [v(13.1, -22.34) * mm, v(12.93, -22.41) * mm, v(12.8, -22.56) * mm, v(12.72, -22.74) * mm]});
            skLineSegment(sketch, "E292", {"start": v(12.72, -22.74) * mm, "end": v(10.62, -28.27) * mm});
            skFitSpline(sketch, "E293", {"points": [v(10.62, -28.27) * mm, v(10.55, -28.47) * mm, v(10.55, -28.64) * mm, v(10.65, -28.82) * mm]});
            skFitSpline(sketch, "E294", {"points": [v(10.65, -28.82) * mm, v(10.72, -29) * mm, v(10.87, -29.12) * mm, v(11.05, -29.2) * mm]});
            skFitSpline(sketch, "E295", {"points": [v(11.05, -29.2) * mm, v(11.25, -29.27) * mm, v(11.42, -29.27) * mm, v(11.62, -29.2) * mm]});
            skFitSpline(sketch, "E296", {"points": [v(11.62, -29.2) * mm, v(11.82, -29.12) * mm, v(11.95, -29) * mm, v(12.02, -28.8) * mm]});
            skLineSegment(sketch, "E297", {"start": v(12.02, -28.8) * mm, "end": v(13.3, -25.44) * mm});
            skFitSpline(sketch, "E298", {"points": [v(13.3, -25.44) * mm, v(13.45, -25.04) * mm, v(13.73, -24.74) * mm, v(14.13, -24.57) * mm]});
            skFitSpline(sketch, "E299", {"points": [v(14.13, -24.57) * mm, v(14.33, -24.47) * mm, v(14.55, -24.42) * mm, v(14.75, -24.42) * mm]});
            skFitSpline(sketch, "E300", {"points": [v(14.75, -24.42) * mm, v(14.95, -24.42) * mm, v(15.13, -24.44) * mm, v(15.33, -24.52) * mm]});
            skFitSpline(sketch, "E301", {"points": [v(15.33, -24.52) * mm, v(15.73, -24.67) * mm, v(16.05, -24.97) * mm, v(16.23, -25.34) * mm]});
            skFitSpline(sketch, "E302", {"points": [v(16.23, -25.34) * mm, v(16.4, -25.74) * mm, v(16.43, -26.14) * mm, v(16.28, -26.57) * mm]});
            skLineSegment(sketch, "E303", {"start": v(16.28, -26.57) * mm, "end": v(15, -29.92) * mm});
            skFitSpline(sketch, "E304", {"points": [v(15, -29.92) * mm, v(14.93, -30.12) * mm, v(14.93, -30.3) * mm, v(15.03, -30.47) * mm]});
            skFitSpline(sketch, "E305", {"points": [v(15.03, -30.47) * mm, v(15.13, -30.67) * mm, v(15.25, -30.8) * mm, v(15.43, -30.84) * mm]});
            skFitSpline(sketch, "E306", {"points": [v(15.43, -30.84) * mm, v(15.6, -30.92) * mm, v(15.8, -30.92) * mm, v(15.98, -30.82) * mm]});
            skFitSpline(sketch, "E307", {"points": [v(15.98, -30.82) * mm, v(16.15, -30.74) * mm, v(16.28, -30.6) * mm, v(16.35, -30.42) * mm]});
            skLineSegment(sketch, "E308", {"start": v(16.35, -30.42) * mm, "end": v(17.63, -27.07) * mm});
            skFitSpline(sketch, "E309", {"points": [v(17.63, -27.07) * mm, v(17.93, -26.3) * mm, v(17.9, -25.52) * mm, v(17.55, -24.74) * mm]});
            skFitSpline(sketch, "E310", {"points": [v(17.55, -24.74) * mm, v(17.2, -23.99) * mm, v(16.63, -23.44) * mm, v(15.83, -23.14) * mm]});
            skFitSpline(sketch, "E311", {"points": [v(27.81, -23.56) * mm, v(27.61, -23.51) * mm, v(27.41, -23.54) * mm, v(27.24, -23.66) * mm]});
            skFitSpline(sketch, "E312", {"points": [v(27.24, -23.66) * mm, v(27.06, -23.76) * mm, v(26.93, -23.91) * mm, v(26.88, -24.12) * mm]});
            skLineSegment(sketch, "E313", {"start": v(26.88, -24.12) * mm, "end": v(26.2, -26.97) * mm});
            skLineSegment(sketch, "E314", {"start": v(26.2, -26.97) * mm, "end": v(26.13, -26.87) * mm});
            skFitSpline(sketch, "E315", {"points": [v(26.13, -26.87) * mm, v(25.66, -26.34) * mm, v(25.06, -25.97) * mm, v(24.36, -25.82) * mm]});
            skFitSpline(sketch, "E316", {"points": [v(24.36, -25.82) * mm, v(23.4, -25.6) * mm, v(22.48, -25.74) * mm, v(21.63, -26.3) * mm]});
            skFitSpline(sketch, "E317", {"points": [v(21.63, -26.3) * mm, v(20.78, -26.84) * mm, v(20.23, -27.62) * mm, v(20, -28.6) * mm]});
            skFitSpline(sketch, "E318", {"points": [v(20, -28.6) * mm, v(19.78, -29.57) * mm, v(19.9, -30.5) * mm, v(20.43, -31.37) * mm]});
            skFitSpline(sketch, "E319", {"points": [v(20.43, -31.37) * mm, v(20.93, -32.22) * mm, v(21.68, -32.8) * mm, v(22.66, -33.02) * mm]});
            skFitSpline(sketch, "E320", {"points": [v(22.66, -33.02) * mm, v(23.36, -33.2) * mm, v(24.06, -33.15) * mm, v(24.76, -32.87) * mm]});
            skLineSegment(sketch, "E321", {"start": v(24.76, -32.87) * mm, "end": v(24.83, -32.85) * mm});
            skLineSegment(sketch, "E322", {"start": v(24.83, -32.85) * mm, "end": v(24.83, -32.95) * mm});
            skFitSpline(sketch, "E323", {"points": [v(24.83, -32.95) * mm, v(24.83, -33.12) * mm, v(24.88, -33.27) * mm, v(24.98, -33.42) * mm]});
            skFitSpline(sketch, "E324", {"points": [v(24.98, -33.42) * mm, v(25.08, -33.57) * mm, v(25.23, -33.65) * mm, v(25.43, -33.7) * mm]});
            skFitSpline(sketch, "E325", {"points": [v(25.43, -33.7) * mm, v(25.63, -33.75) * mm, v(25.8, -33.72) * mm, v(25.98, -33.6) * mm]});
            skFitSpline(sketch, "E326", {"points": [v(25.98, -33.6) * mm, v(26.16, -33.5) * mm, v(26.28, -33.35) * mm, v(26.33, -33.15) * mm]});
            skLineSegment(sketch, "E327", {"start": v(26.33, -33.15) * mm, "end": v(28.41, -24.52) * mm});
            skFitSpline(sketch, "E328", {"points": [v(28.41, -24.52) * mm, v(28.46, -24.32) * mm, v(28.44, -24.14) * mm, v(28.31, -23.94) * mm]});
            skFitSpline(sketch, "E329", {"points": [v(28.31, -23.94) * mm, v(28.19, -23.71) * mm, v(28.04, -23.59) * mm, v(27.81, -23.56) * mm]});
            skFitSpline(sketch, "E330", {"points": [v(25.53, -29.9) * mm, v(25.4, -30.47) * mm, v(25.08, -30.92) * mm, v(24.58, -31.25) * mm]});
            skFitSpline(sketch, "E331", {"points": [v(24.58, -31.25) * mm, v(24.23, -31.47) * mm, v(23.86, -31.6) * mm, v(23.48, -31.6) * mm]});
            skFitSpline(sketch, "E332", {"points": [v(23.48, -31.6) * mm, v(23.33, -31.6) * mm, v(23.16, -31.57) * mm, v(23, -31.55) * mm]});
            skFitSpline(sketch, "E333", {"points": [v(23, -31.55) * mm, v(22.46, -31.42) * mm, v(22.03, -31.1) * mm, v(21.73, -30.57) * mm]});
            skFitSpline(sketch, "E334", {"points": [v(21.73, -30.57) * mm, v(21.43, -30.07) * mm, v(21.36, -29.52) * mm, v(21.48, -28.94) * mm]});
            skFitSpline(sketch, "E335", {"points": [v(21.48, -28.94) * mm, v(21.6, -28.37) * mm, v(21.93, -27.92) * mm, v(22.43, -27.6) * mm]});
            skFitSpline(sketch, "E336", {"points": [v(22.43, -27.6) * mm, v(22.93, -27.27) * mm, v(23.46, -27.17) * mm, v(24, -27.3) * mm]});
            skFitSpline(sketch, "E337", {"points": [v(24, -27.3) * mm, v(24.56, -27.42) * mm, v(25, -27.74) * mm, v(25.28, -28.27) * mm]});
            skFitSpline(sketch, "E338", {"points": [v(25.28, -28.27) * mm, v(25.58, -28.77) * mm, v(25.66, -29.32) * mm, v(25.53, -29.9) * mm]});
            skFitSpline(sketch, "E339", {"points": [v(36.74, -28.37) * mm, v(36.72, -28.34) * mm, v(36.72, -28.32) * mm, v(36.72, -28.27) * mm]});
            skFitSpline(sketch, "E340", {"points": [v(36.72, -28.27) * mm, v(36.72, -28.25) * mm, v(36.7, -28.2) * mm, v(36.7, -28.14) * mm]});
            skFitSpline(sketch, "E341", {"points": [v(36.7, -28.14) * mm, v(36.67, -28.12) * mm, v(36.64, -28.1) * mm, v(36.62, -28.04) * mm]});
            skFitSpline(sketch, "E342", {"points": [v(36.62, -28.04) * mm, v(36.6, -28.03) * mm, v(36.6, -28) * mm, v(36.6, -28) * mm]});
            skLineSegment(sketch, "E343", {"start": v(36.6, -28) * mm, "end": v(36.57, -28) * mm});
            skLineSegment(sketch, "E344", {"start": v(36.57, -28) * mm, "end": v(36.5, -27.87) * mm});
            skLineSegment(sketch, "E345", {"start": v(36.5, -27.87) * mm, "end": v(36.4, -27.8) * mm});
            skFitSpline(sketch, "E346", {"points": [v(36.4, -27.8) * mm, v(36.37, -27.8) * mm, v(36.34, -27.77) * mm, v(36.34, -27.74) * mm]});
            skFitSpline(sketch, "E347", {"points": [v(36.34, -27.74) * mm, v(36.32, -27.72) * mm, v(36.3, -27.72) * mm, v(36.27, -27.7) * mm]});
            skLineSegment(sketch, "E348", {"start": v(36.24, -27.7) * mm, "end": v(36.17, -27.7) * mm});
            skLineSegment(sketch, "E349", {"start": v(36.17, -27.7) * mm, "end": v(36.07, -27.67) * mm});
            skLineSegment(sketch, "E350", {"start": v(36.07, -27.67) * mm, "end": v(31.76, -27.22) * mm});
            skFitSpline(sketch, "E351", {"points": [v(31.76, -27.22) * mm, v(31.56, -27.2) * mm, v(31.39, -27.24) * mm, v(31.24, -27.37) * mm]});
            skFitSpline(sketch, "E352", {"points": [v(31.24, -27.37) * mm, v(31.06, -27.5) * mm, v(30.99, -27.67) * mm, v(30.96, -27.87) * mm]});
            skFitSpline(sketch, "E353", {"points": [v(30.96, -27.87) * mm, v(30.94, -28.07) * mm, v(30.99, -28.24) * mm, v(31.14, -28.4) * mm]});
            skFitSpline(sketch, "E354", {"points": [v(31.14, -28.4) * mm, v(31.26, -28.54) * mm, v(31.44, -28.64) * mm, v(31.61, -28.67) * mm]});
            skLineSegment(sketch, "E355", {"start": v(31.61, -28.67) * mm, "end": v(34.47, -28.97) * mm});
            skLineSegment(sketch, "E356", {"start": v(34.47, -28.97) * mm, "end": v(30.54, -33.4) * mm});
            skLineSegment(sketch, "E357", {"start": v(30.54, -33.4) * mm, "end": v(30.51, -33.4) * mm});
            skLineSegment(sketch, "E358", {"start": v(30.51, -33.4) * mm, "end": v(30.51, -33.45) * mm});
            skLineSegment(sketch, "E359", {"start": v(30.51, -33.45) * mm, "end": v(30.49, -33.45) * mm});
            skFitSpline(sketch, "E360", {"points": [v(30.49, -33.45) * mm, v(30.45, -33.46) * mm, v(30.44, -33.49) * mm, v(30.44, -33.52) * mm]});
            skFitSpline(sketch, "E361", {"points": [v(30.44, -33.52) * mm, v(30.44, -33.57) * mm, v(30.41, -33.6) * mm, v(30.39, -33.62) * mm]});
            skLineSegment(sketch, "E362", {"start": v(30.39, -33.62) * mm, "end": v(30.39, -33.67) * mm});
            skLineSegment(sketch, "E363", {"start": v(30.39, -33.67) * mm, "end": v(30.36, -33.77) * mm});
            skLineSegment(sketch, "E364", {"start": v(30.36, -33.77) * mm, "end": v(30.39, -33.8) * mm});
            skLineSegment(sketch, "E365", {"start": v(30.39, -33.8) * mm, "end": v(30.39, -33.92) * mm});
            skLineSegment(sketch, "E366", {"start": v(30.39, -33.92) * mm, "end": v(30.41, -34.07) * mm});
            skLineSegment(sketch, "E367", {"start": v(30.41, -34.07) * mm, "end": v(30.46, -34.12) * mm});
            skLineSegment(sketch, "E368", {"start": v(30.46, -34.12) * mm, "end": v(30.46, -34.17) * mm});
            skFitSpline(sketch, "E369", {"points": [v(30.46, -34.17) * mm, v(30.46, -34.19) * mm, v(30.49, -34.23) * mm, v(30.54, -34.3) * mm]});
            skFitSpline(sketch, "E370", {"points": [v(30.54, -34.3) * mm, v(30.57, -34.36) * mm, v(30.6, -34.4) * mm, v(30.64, -34.4) * mm]});
            skLineSegment(sketch, "E371", {"start": v(30.64, -34.4) * mm, "end": v(30.71, -34.4) * mm});
            skLineSegment(sketch, "E372", {"start": v(30.71, -34.4) * mm, "end": v(30.71, -34.45) * mm});
            skLineSegment(sketch, "E373", {"start": v(30.74, -34.47) * mm, "end": v(30.84, -34.52) * mm});
            skFitSpline(sketch, "E374", {"points": [v(30.84, -34.52) * mm, v(30.85, -34.52) * mm, v(30.88, -34.53) * mm, v(30.91, -34.55) * mm]});
            skLineSegment(sketch, "E375", {"start": v(30.91, -34.55) * mm, "end": v(30.94, -34.55) * mm});
            skFitSpline(sketch, "E376", {"points": [v(30.94, -34.55) * mm, v(30.99, -34.57) * mm, v(31.04, -34.57) * mm, v(31.09, -34.57) * mm]});
            skLineSegment(sketch, "E377", {"start": v(31.09, -34.57) * mm, "end": v(35.4, -35.02) * mm});
            skFitSpline(sketch, "E378", {"points": [v(35.4, -35.02) * mm, v(35.6, -35.05) * mm, v(35.77, -35) * mm, v(35.92, -34.87) * mm]});
            skFitSpline(sketch, "E379", {"points": [v(35.92, -34.87) * mm, v(36.1, -34.75) * mm, v(36.17, -34.57) * mm, v(36.2, -34.37) * mm]});
            skFitSpline(sketch, "E380", {"points": [v(36.2, -34.37) * mm, v(36.22, -34.17) * mm, v(36.17, -34) * mm, v(36.02, -33.85) * mm]});
            skFitSpline(sketch, "E381", {"points": [v(36.02, -33.85) * mm, v(35.9, -33.7) * mm, v(35.72, -33.6) * mm, v(35.54, -33.57) * mm]});
            skLineSegment(sketch, "E382", {"start": v(35.54, -33.57) * mm, "end": v(32.66, -33.27) * mm});
            skLineSegment(sketch, "E383", {"start": v(32.66, -33.27) * mm, "end": v(36.6, -28.87) * mm});
            skLineSegment(sketch, "E384", {"start": v(36.6, -28.87) * mm, "end": v(36.64, -28.82) * mm});
            skLineSegment(sketch, "E385", {"start": v(36.64, -28.82) * mm, "end": v(36.64, -28.74) * mm});
            skLineSegment(sketch, "E386", {"start": v(36.64, -28.74) * mm, "end": v(36.7, -28.74) * mm});
            skLineSegment(sketch, "E387", {"start": v(36.7, -28.74) * mm, "end": v(36.7, -28.7) * mm});
            skFitSpline(sketch, "E388", {"points": [v(36.7, -28.7) * mm, v(36.72, -28.67) * mm, v(36.72, -28.62) * mm, v(36.72, -28.57) * mm]});
            skLineSegment(sketch, "E389", {"start": v(36.72, -28.57) * mm, "end": v(36.74, -28.5) * mm});
            skLineSegment(sketch, "E390", {"start": v(36.74, -28.5) * mm, "end": v(36.74, -28.44) * mm});
            skLineSegment(sketch, "E391", {"start": v(36.74, -28.44) * mm, "end": v(36.74, -28.37) * mm});
            skArc(sketch, "E392", {"start": v(-39.94, 40.51) * mm, "mid": v(-16.5, -16.05) * mm, "end": v(40.06, -39.49) * mm});
            skLineSegment(sketch, "E393", {"start": v(30.71, -34.45) * mm, "end": v(30.73, -34.47) * mm});
            skLineSegment(sketch, "E394", {"start": v(30.73, -34.47) * mm, "end": v(30.74, -34.47) * mm});
            skLineSegment(sketch, "E395", {"start": v(-39.94, 40.51) * mm, "end": v(40.06, 40.51) * mm});
            skLineSegment(sketch, "E396", {"start": v(40.06, 40.51) * mm, "end": v(40.06, -39.49) * mm});
            skLineSegment(sketch, "E397", {"start": v(36.24, -27.7) * mm, "end": v(36.27, -27.7) * mm});
            skLineSegment(sketch, "E398", {"start": v(30.84, -34.52) * mm, "end": v(30.84, -34.52) * mm});
            skSolve(sketch);
        }
        {
            var Q0;
            Q0=qSketchRegion(id+"F0",true);
            var Q1;
            Q1=makeQuery(id+"F0.imprint","IMPRINT",FACE,{"disambiguationData":[TD([[makeQuery(id+"F0.imprint","IMPRINT",EDGE,{"derivedFrom":sQuery(id+"F0.wireOp",EDGE,"E41")}),1.0]])]});
            var Q2;
            Q2=makeQuery(id+"F0.imprint","IMPRINT",FACE,{"disambiguationData":[TD([[makeQuery(id+"F0.imprint","IMPRINT",EDGE,{"derivedFrom":sQuery(id+"F0.wireOp",EDGE,"E78")}),1.0]])]});
            var Q3;
            Q3=makeQuery(id+"F0.imprint","IMPRINT",FACE,{"disambiguationData":[TD([[makeQuery(id+"F0.imprint","IMPRINT",EDGE,{"derivedFrom":sQuery(id+"F0.wireOp",EDGE,"E118")}),1.0]])]});
            var Q4;
            Q4=makeQuery(id+"F0.imprint","IMPRINT",FACE,{"disambiguationData":[TD([[makeQuery(id+"F0.imprint","IMPRINT",EDGE,{"derivedFrom":sQuery(id+"F0.wireOp",EDGE,"E134")}),-1.0]])]});
            var Q5;
            Q5=makeQuery(id+"F0.imprint","IMPRINT",FACE,{"disambiguationData":[TD([[makeQuery(id+"F0.imprint","IMPRINT",EDGE,{"derivedFrom":sQuery(id+"F0.wireOp",EDGE,"E21")}),1.0]])]});
            var Q6;
            Q6=makeQuery(id+"F0.imprint","IMPRINT",FACE,{"disambiguationData":[TD([[makeQuery(id+"F0.imprint","IMPRINT",EDGE,{"derivedFrom":sQuery(id+"F0.wireOp",EDGE,"E0")}),1.0]])]});
            var Q7;
            Q7=makeQuery(id+"F0.imprint","IMPRINT",FACE,{"disambiguationData":[TD([[makeQuery(id+"F0.imprint","IMPRINT",EDGE,{"derivedFrom":sQuery(id+"F0.wireOp",EDGE,"E143")}),1.0]])]});
            var Q8;
            Q8=makeQuery(id+"F0.imprint","IMPRINT",FACE,{"disambiguationData":[TD([[makeQuery(id+"F0.imprint","IMPRINT",EDGE,{"derivedFrom":sQuery(id+"F0.wireOp",EDGE,"E161")}),1.0]])]});
            var Q9;
            Q9=makeQuery(id+"F0.imprint","IMPRINT",FACE,{"disambiguationData":[TD([[makeQuery(id+"F0.imprint","IMPRINT",EDGE,{"derivedFrom":sQuery(id+"F0.wireOp",EDGE,"E188")}),1.0]])]});
            var Q10;
            Q10=makeQuery(id+"F0.imprint","IMPRINT",FACE,{"disambiguationData":[TD([[makeQuery(id+"F0.imprint","IMPRINT",EDGE,{"derivedFrom":sQuery(id+"F0.wireOp",EDGE,"E218")}),1.0]])]});
            var Q11;
            Q11=makeQuery(id+"F0.imprint","IMPRINT",FACE,{"disambiguationData":[TD([[makeQuery(id+"F0.imprint","IMPRINT",EDGE,{"derivedFrom":sQuery(id+"F0.wireOp",EDGE,"E238")}),1.0]])]});
            var Q12;
            Q12=makeQuery(id+"F0.imprint","IMPRINT",FACE,{"disambiguationData":[TD([[makeQuery(id+"F0.imprint","IMPRINT",EDGE,{"derivedFrom":sQuery(id+"F0.wireOp",EDGE,"E249")}),1.0]])]});
            var Q13;
            Q13=makeQuery(id+"F0.imprint","IMPRINT",FACE,{"disambiguationData":[TD([[makeQuery(id+"F0.imprint","IMPRINT",EDGE,{"derivedFrom":sQuery(id+"F0.wireOp",EDGE,"E260")}),1.0]])]});
            var Q14;
            Q14=makeQuery(id+"F0.imprint","IMPRINT",FACE,{"disambiguationData":[TD([[makeQuery(id+"F0.imprint","IMPRINT",EDGE,{"derivedFrom":sQuery(id+"F0.wireOp",EDGE,"E279")}),-1.0]])]});
            var Q15;
            Q15=makeQuery(id+"F0.imprint","IMPRINT",FACE,{"disambiguationData":[TD([[makeQuery(id+"F0.imprint","IMPRINT",EDGE,{"derivedFrom":sQuery(id+"F0.wireOp",EDGE,"E286")}),1.0]])]});
            var Q16;
            Q16=makeQuery(id+"F0.imprint","IMPRINT",FACE,{"disambiguationData":[TD([[makeQuery(id+"F0.imprint","IMPRINT",EDGE,{"derivedFrom":sQuery(id+"F0.wireOp",EDGE,"E330")}),-1.0]])]});
            var Q17;
            Q17=makeQuery(id+"F0.imprint","IMPRINT",FACE,{"disambiguationData":[TD([[makeQuery(id+"F0.imprint","IMPRINT",EDGE,{"derivedFrom":sQuery(id+"F0.wireOp",EDGE,"E311")}),1.0]])]});
            var Q18;
            Q18=makeQuery(id+"F0.imprint","IMPRINT",FACE,{"disambiguationData":[TD([[makeQuery(id+"F0.imprint","IMPRINT",EDGE,{"derivedFrom":sQuery(id+"F0.wireOp",EDGE,"E339")}),1.0]])]});
            extrude(context, id + "F1", {"entities" : qUnion([Q0, Q1, Q2, Q3, Q4, Q5, Q6, Q7, Q8, Q9, Q10, Q11, Q12, Q13, Q14, Q15, Q16, Q17, Q18]), "oppositeDirection" : true, "depth" : 2 * mm});
        }
        {
            var Q0;
            Q0=makeQuery(id+"F0.imprint","IMPRINT",FACE,{"disambiguationData":[TD([[makeQuery(id+"F0.imprint","IMPRINT",EDGE,{"derivedFrom":sQuery(id+"F0.wireOp",EDGE,"E0")}),-1.0]])]});
            var Q1;
            Q1=makeQuery(id+"F0.imprint","IMPRINT",FACE,{"disambiguationData":[TD([[makeQuery(id+"F0.imprint","IMPRINT",EDGE,{"derivedFrom":sQuery(id+"F0.wireOp",EDGE,"E330")}),-1.0]])]});
            var Q2;
            Q2=makeQuery(id+"F0.imprint","IMPRINT",FACE,{"disambiguationData":[TD([[makeQuery(id+"F0.imprint","IMPRINT",EDGE,{"derivedFrom":sQuery(id+"F0.wireOp",EDGE,"E279")}),-1.0]])]});
            var Q3;
            Q3=makeQuery(id+"F0.imprint","IMPRINT",FACE,{"disambiguationData":[TD([[makeQuery(id+"F0.imprint","IMPRINT",EDGE,{"derivedFrom":sQuery(id+"F0.wireOp",EDGE,"E134")}),-1.0]])]});
            extrude(context, id + "F2", {"entities" : qUnion([Q0, Q1, Q2, Q3]), "operationType" : NewBodyOperationType.ADD, "depth" : 2 * mm});
        }
        {
            var Q0;
            Q0=makeQuery(id+"F2.opExtrude","CAP_FACE",FACE,{"disambiguationData":[OSD([sQuery(id+"F0.wireOp",EDGE,"E0"),sQuery(id+"F0.wireOp",EDGE,"E1"),sQuery(id+"F0.wireOp",EDGE,"E2"),sQuery(id+"F0.wireOp",EDGE,"E3"),sQuery(id+"F0.wireOp",EDGE,"E4"),sQuery(id+"F0.wireOp",EDGE,"E5"),sQuery(id+"F0.wireOp",EDGE,"E6"),sQuery(id+"F0.wireOp",EDGE,"E7"),sQuery(id+"F0.wireOp",EDGE,"E8"),sQuery(id+"F0.wireOp",EDGE,"E9"),sQuery(id+"F0.wireOp",EDGE,"E10"),sQuery(id+"F0.wireOp",EDGE,"E11"),sQuery(id+"F0.wireOp",EDGE,"E12"),sQuery(id+"F0.wireOp",EDGE,"E13"),sQuery(id+"F0.wireOp",EDGE,"E14"),sQuery(id+"F0.wireOp",EDGE,"E15"),sQuery(id+"F0.wireOp",EDGE,"E16"),sQuery(id+"F0.wireOp",EDGE,"E17"),sQuery(id+"F0.wireOp",EDGE,"E18"),sQuery(id+"F0.wireOp",EDGE,"E19"),sQuery(id+"F0.wireOp",EDGE,"E20"),sQuery(id+"F0.wireOp",EDGE,"E21"),sQuery(id+"F0.wireOp",EDGE,"E22"),sQuery(id+"F0.wireOp",EDGE,"E23"),sQuery(id+"F0.wireOp",EDGE,"E24"),sQuery(id+"F0.wireOp",EDGE,"E25"),sQuery(id+"F0.wireOp",EDGE,"E26"),sQuery(id+"F0.wireOp",EDGE,"E27"),sQuery(id+"F0.wireOp",EDGE,"E28"),sQuery(id+"F0.wireOp",EDGE,"E29"),sQuery(id+"F0.wireOp",EDGE,"E30"),sQuery(id+"F0.wireOp",EDGE,"E31"),sQuery(id+"F0.wireOp",EDGE,"E32"),sQuery(id+"F0.wireOp",EDGE,"E33"),sQuery(id+"F0.wireOp",EDGE,"E34"),sQuery(id+"F0.wireOp",EDGE,"E35"),sQuery(id+"F0.wireOp",EDGE,"E36"),sQuery(id+"F0.wireOp",EDGE,"E37"),sQuery(id+"F0.wireOp",EDGE,"E38"),sQuery(id+"F0.wireOp",EDGE,"E39"),sQuery(id+"F0.wireOp",EDGE,"E40"),sQuery(id+"F0.wireOp",EDGE,"E41"),sQuery(id+"F0.wireOp",EDGE,"E42"),sQuery(id+"F0.wireOp",EDGE,"E43"),sQuery(id+"F0.wireOp",EDGE,"E44"),sQuery(id+"F0.wireOp",EDGE,"E45"),sQuery(id+"F0.wireOp",EDGE,"E46"),sQuery(id+"F0.wireOp",EDGE,"E47"),sQuery(id+"F0.wireOp",EDGE,"E48"),sQuery(id+"F0.wireOp",EDGE,"E49"),sQuery(id+"F0.wireOp",EDGE,"E50"),sQuery(id+"F0.wireOp",EDGE,"E51"),sQuery(id+"F0.wireOp",EDGE,"E52"),sQuery(id+"F0.wireOp",EDGE,"E53"),sQuery(id+"F0.wireOp",EDGE,"E54"),sQuery(id+"F0.wireOp",EDGE,"E55"),sQuery(id+"F0.wireOp",EDGE,"E56"),sQuery(id+"F0.wireOp",EDGE,"E57"),sQuery(id+"F0.wireOp",EDGE,"E58"),sQuery(id+"F0.wireOp",EDGE,"E59"),sQuery(id+"F0.wireOp",EDGE,"E60"),sQuery(id+"F0.wireOp",EDGE,"E61"),sQuery(id+"F0.wireOp",EDGE,"E62"),sQuery(id+"F0.wireOp",EDGE,"E63"),sQuery(id+"F0.wireOp",EDGE,"E64"),sQuery(id+"F0.wireOp",EDGE,"E65"),sQuery(id+"F0.wireOp",EDGE,"E66"),sQuery(id+"F0.wireOp",EDGE,"E67"),sQuery(id+"F0.wireOp",EDGE,"E68"),sQuery(id+"F0.wireOp",EDGE,"E69"),sQuery(id+"F0.wireOp",EDGE,"E70"),sQuery(id+"F0.wireOp",EDGE,"E71"),sQuery(id+"F0.wireOp",EDGE,"E72"),sQuery(id+"F0.wireOp",EDGE,"E73"),sQuery(id+"F0.wireOp",EDGE,"E74"),sQuery(id+"F0.wireOp",EDGE,"E75"),sQuery(id+"F0.wireOp",EDGE,"E76"),sQuery(id+"F0.wireOp",EDGE,"E77"),sQuery(id+"F0.wireOp",EDGE,"E78"),sQuery(id+"F0.wireOp",EDGE,"E79"),sQuery(id+"F0.wireOp",EDGE,"E80"),sQuery(id+"F0.wireOp",EDGE,"E81"),sQuery(id+"F0.wireOp",EDGE,"E82"),sQuery(id+"F0.wireOp",EDGE,"E83"),sQuery(id+"F0.wireOp",EDGE,"E84"),sQuery(id+"F0.wireOp",EDGE,"E85"),sQuery(id+"F0.wireOp",EDGE,"E86"),sQuery(id+"F0.wireOp",EDGE,"E87"),sQuery(id+"F0.wireOp",EDGE,"E88"),sQuery(id+"F0.wireOp",EDGE,"E89"),sQuery(id+"F0.wireOp",EDGE,"E90"),sQuery(id+"F0.wireOp",EDGE,"E91"),sQuery(id+"F0.wireOp",EDGE,"E92"),sQuery(id+"F0.wireOp",EDGE,"E93"),sQuery(id+"F0.wireOp",EDGE,"E94"),sQuery(id+"F0.wireOp",EDGE,"E95"),sQuery(id+"F0.wireOp",EDGE,"E96"),sQuery(id+"F0.wireOp",EDGE,"E97"),sQuery(id+"F0.wireOp",EDGE,"E98"),sQuery(id+"F0.wireOp",EDGE,"E99"),sQuery(id+"F0.wireOp",EDGE,"E100"),sQuery(id+"F0.wireOp",EDGE,"E101"),sQuery(id+"F0.wireOp",EDGE,"E102"),sQuery(id+"F0.wireOp",EDGE,"E103"),sQuery(id+"F0.wireOp",EDGE,"E104"),sQuery(id+"F0.wireOp",EDGE,"E105"),sQuery(id+"F0.wireOp",EDGE,"E106"),sQuery(id+"F0.wireOp",EDGE,"E107"),sQuery(id+"F0.wireOp",EDGE,"E108"),sQuery(id+"F0.wireOp",EDGE,"E109"),sQuery(id+"F0.wireOp",EDGE,"E110"),sQuery(id+"F0.wireOp",EDGE,"E111"),sQuery(id+"F0.wireOp",EDGE,"E112"),sQuery(id+"F0.wireOp",EDGE,"E113"),sQuery(id+"F0.wireOp",EDGE,"E114"),sQuery(id+"F0.wireOp",EDGE,"E115"),sQuery(id+"F0.wireOp",EDGE,"E116"),sQuery(id+"F0.wireOp",EDGE,"E117"),sQuery(id+"F0.wireOp",EDGE,"E118"),sQuery(id+"F0.wireOp",EDGE,"E119"),sQuery(id+"F0.wireOp",EDGE,"E120"),sQuery(id+"F0.wireOp",EDGE,"E121"),sQuery(id+"F0.wireOp",EDGE,"E122"),sQuery(id+"F0.wireOp",EDGE,"E123"),sQuery(id+"F0.wireOp",EDGE,"E124"),sQuery(id+"F0.wireOp",EDGE,"E125"),sQuery(id+"F0.wireOp",EDGE,"E126"),sQuery(id+"F0.wireOp",EDGE,"E127"),sQuery(id+"F0.wireOp",EDGE,"E128"),sQuery(id+"F0.wireOp",EDGE,"E129"),sQuery(id+"F0.wireOp",EDGE,"E130"),sQuery(id+"F0.wireOp",EDGE,"E131"),sQuery(id+"F0.wireOp",EDGE,"E132"),sQuery(id+"F0.wireOp",EDGE,"E133"),sQuery(id+"F0.wireOp",EDGE,"E143"),sQuery(id+"F0.wireOp",EDGE,"E144"),sQuery(id+"F0.wireOp",EDGE,"E145"),sQuery(id+"F0.wireOp",EDGE,"E146"),sQuery(id+"F0.wireOp",EDGE,"E147"),sQuery(id+"F0.wireOp",EDGE,"E148"),sQuery(id+"F0.wireOp",EDGE,"E149"),sQuery(id+"F0.wireOp",EDGE,"E150"),sQuery(id+"F0.wireOp",EDGE,"E151"),sQuery(id+"F0.wireOp",EDGE,"E152"),sQuery(id+"F0.wireOp",EDGE,"E153"),sQuery(id+"F0.wireOp",EDGE,"E154"),sQuery(id+"F0.wireOp",EDGE,"E155"),sQuery(id+"F0.wireOp",EDGE,"E156"),sQuery(id+"F0.wireOp",EDGE,"E157"),sQuery(id+"F0.wireOp",EDGE,"E158"),sQuery(id+"F0.wireOp",EDGE,"E159"),sQuery(id+"F0.wireOp",EDGE,"E160"),sQuery(id+"F0.wireOp",EDGE,"E161"),sQuery(id+"F0.wireOp",EDGE,"E162"),sQuery(id+"F0.wireOp",EDGE,"E163"),sQuery(id+"F0.wireOp",EDGE,"E164"),sQuery(id+"F0.wireOp",EDGE,"E165"),sQuery(id+"F0.wireOp",EDGE,"E166"),sQuery(id+"F0.wireOp",EDGE,"E167"),sQuery(id+"F0.wireOp",EDGE,"E168"),sQuery(id+"F0.wireOp",EDGE,"E169"),sQuery(id+"F0.wireOp",EDGE,"E170"),sQuery(id+"F0.wireOp",EDGE,"E171"),sQuery(id+"F0.wireOp",EDGE,"E172"),sQuery(id+"F0.wireOp",EDGE,"E173"),sQuery(id+"F0.wireOp",EDGE,"E174"),sQuery(id+"F0.wireOp",EDGE,"E175"),sQuery(id+"F0.wireOp",EDGE,"E176"),sQuery(id+"F0.wireOp",EDGE,"E177"),sQuery(id+"F0.wireOp",EDGE,"E178"),sQuery(id+"F0.wireOp",EDGE,"E179"),sQuery(id+"F0.wireOp",EDGE,"E180"),sQuery(id+"F0.wireOp",EDGE,"E181"),sQuery(id+"F0.wireOp",EDGE,"E182"),sQuery(id+"F0.wireOp",EDGE,"E183"),sQuery(id+"F0.wireOp",EDGE,"E184"),sQuery(id+"F0.wireOp",EDGE,"E185"),sQuery(id+"F0.wireOp",EDGE,"E186"),sQuery(id+"F0.wireOp",EDGE,"E187"),sQuery(id+"F0.wireOp",EDGE,"E188"),sQuery(id+"F0.wireOp",EDGE,"E189"),sQuery(id+"F0.wireOp",EDGE,"E190"),sQuery(id+"F0.wireOp",EDGE,"E191"),sQuery(id+"F0.wireOp",EDGE,"E192"),sQuery(id+"F0.wireOp",EDGE,"E193"),sQuery(id+"F0.wireOp",EDGE,"E194"),sQuery(id+"F0.wireOp",EDGE,"E195"),sQuery(id+"F0.wireOp",EDGE,"E196"),sQuery(id+"F0.wireOp",EDGE,"E197"),sQuery(id+"F0.wireOp",EDGE,"E198"),sQuery(id+"F0.wireOp",EDGE,"E199"),sQuery(id+"F0.wireOp",EDGE,"E200"),sQuery(id+"F0.wireOp",EDGE,"E201"),sQuery(id+"F0.wireOp",EDGE,"E202"),sQuery(id+"F0.wireOp",EDGE,"E203"),sQuery(id+"F0.wireOp",EDGE,"E204"),sQuery(id+"F0.wireOp",EDGE,"E205"),sQuery(id+"F0.wireOp",EDGE,"E206"),sQuery(id+"F0.wireOp",EDGE,"E207"),sQuery(id+"F0.wireOp",EDGE,"E208"),sQuery(id+"F0.wireOp",EDGE,"E209"),sQuery(id+"F0.wireOp",EDGE,"E210"),sQuery(id+"F0.wireOp",EDGE,"E211"),sQuery(id+"F0.wireOp",EDGE,"E212"),sQuery(id+"F0.wireOp",EDGE,"E213"),sQuery(id+"F0.wireOp",EDGE,"E214"),sQuery(id+"F0.wireOp",EDGE,"E215"),sQuery(id+"F0.wireOp",EDGE,"E216"),sQuery(id+"F0.wireOp",EDGE,"E217"),sQuery(id+"F0.wireOp",EDGE,"E218"),sQuery(id+"F0.wireOp",EDGE,"E219"),sQuery(id+"F0.wireOp",EDGE,"E220"),sQuery(id+"F0.wireOp",EDGE,"E221"),sQuery(id+"F0.wireOp",EDGE,"E222"),sQuery(id+"F0.wireOp",EDGE,"E223"),sQuery(id+"F0.wireOp",EDGE,"E224"),sQuery(id+"F0.wireOp",EDGE,"E225"),sQuery(id+"F0.wireOp",EDGE,"E226"),sQuery(id+"F0.wireOp",EDGE,"E227"),sQuery(id+"F0.wireOp",EDGE,"E228"),sQuery(id+"F0.wireOp",EDGE,"E229"),sQuery(id+"F0.wireOp",EDGE,"E230"),sQuery(id+"F0.wireOp",EDGE,"E231"),sQuery(id+"F0.wireOp",EDGE,"E232"),sQuery(id+"F0.wireOp",EDGE,"E233"),sQuery(id+"F0.wireOp",EDGE,"E234"),sQuery(id+"F0.wireOp",EDGE,"E235"),sQuery(id+"F0.wireOp",EDGE,"E236"),sQuery(id+"F0.wireOp",EDGE,"E237"),sQuery(id+"F0.wireOp",EDGE,"E238"),sQuery(id+"F0.wireOp",EDGE,"E239"),sQuery(id+"F0.wireOp",EDGE,"E240"),sQuery(id+"F0.wireOp",EDGE,"E241"),sQuery(id+"F0.wireOp",EDGE,"E242"),sQuery(id+"F0.wireOp",EDGE,"E243"),sQuery(id+"F0.wireOp",EDGE,"E244"),sQuery(id+"F0.wireOp",EDGE,"E245"),sQuery(id+"F0.wireOp",EDGE,"E246"),sQuery(id+"F0.wireOp",EDGE,"E247"),sQuery(id+"F0.wireOp",EDGE,"E248"),sQuery(id+"F0.wireOp",EDGE,"E249"),sQuery(id+"F0.wireOp",EDGE,"E250"),sQuery(id+"F0.wireOp",EDGE,"E251"),sQuery(id+"F0.wireOp",EDGE,"E252"),sQuery(id+"F0.wireOp",EDGE,"E253"),sQuery(id+"F0.wireOp",EDGE,"E254"),sQuery(id+"F0.wireOp",EDGE,"E255"),sQuery(id+"F0.wireOp",EDGE,"E256"),sQuery(id+"F0.wireOp",EDGE,"E257"),sQuery(id+"F0.wireOp",EDGE,"E258"),sQuery(id+"F0.wireOp",EDGE,"E259"),sQuery(id+"F0.wireOp",EDGE,"E260"),sQuery(id+"F0.wireOp",EDGE,"E261"),sQuery(id+"F0.wireOp",EDGE,"E262"),sQuery(id+"F0.wireOp",EDGE,"E263"),sQuery(id+"F0.wireOp",EDGE,"E264"),sQuery(id+"F0.wireOp",EDGE,"E265"),sQuery(id+"F0.wireOp",EDGE,"E266"),sQuery(id+"F0.wireOp",EDGE,"E267"),sQuery(id+"F0.wireOp",EDGE,"E268"),sQuery(id+"F0.wireOp",EDGE,"E269"),sQuery(id+"F0.wireOp",EDGE,"E270"),sQuery(id+"F0.wireOp",EDGE,"E271"),sQuery(id+"F0.wireOp",EDGE,"E272"),sQuery(id+"F0.wireOp",EDGE,"E273"),sQuery(id+"F0.wireOp",EDGE,"E274"),sQuery(id+"F0.wireOp",EDGE,"E275"),sQuery(id+"F0.wireOp",EDGE,"E276"),sQuery(id+"F0.wireOp",EDGE,"E277"),sQuery(id+"F0.wireOp",EDGE,"E278"),sQuery(id+"F0.wireOp",EDGE,"E286"),sQuery(id+"F0.wireOp",EDGE,"E287"),sQuery(id+"F0.wireOp",EDGE,"E288"),sQuery(id+"F0.wireOp",EDGE,"E289"),sQuery(id+"F0.wireOp",EDGE,"E290"),sQuery(id+"F0.wireOp",EDGE,"E291"),sQuery(id+"F0.wireOp",EDGE,"E292"),sQuery(id+"F0.wireOp",EDGE,"E293"),sQuery(id+"F0.wireOp",EDGE,"E294"),sQuery(id+"F0.wireOp",EDGE,"E295"),sQuery(id+"F0.wireOp",EDGE,"E296"),sQuery(id+"F0.wireOp",EDGE,"E297"),sQuery(id+"F0.wireOp",EDGE,"E298"),sQuery(id+"F0.wireOp",EDGE,"E299"),sQuery(id+"F0.wireOp",EDGE,"E300"),sQuery(id+"F0.wireOp",EDGE,"E301"),sQuery(id+"F0.wireOp",EDGE,"E302"),sQuery(id+"F0.wireOp",EDGE,"E303"),sQuery(id+"F0.wireOp",EDGE,"E304"),sQuery(id+"F0.wireOp",EDGE,"E305"),sQuery(id+"F0.wireOp",EDGE,"E306"),sQuery(id+"F0.wireOp",EDGE,"E307"),sQuery(id+"F0.wireOp",EDGE,"E308"),sQuery(id+"F0.wireOp",EDGE,"E309"),sQuery(id+"F0.wireOp",EDGE,"E310"),sQuery(id+"F0.wireOp",EDGE,"E311"),sQuery(id+"F0.wireOp",EDGE,"E312"),sQuery(id+"F0.wireOp",EDGE,"E313"),sQuery(id+"F0.wireOp",EDGE,"E314"),sQuery(id+"F0.wireOp",EDGE,"E315"),sQuery(id+"F0.wireOp",EDGE,"E316"),sQuery(id+"F0.wireOp",EDGE,"E317"),sQuery(id+"F0.wireOp",EDGE,"E318"),sQuery(id+"F0.wireOp",EDGE,"E319"),sQuery(id+"F0.wireOp",EDGE,"E320"),sQuery(id+"F0.wireOp",EDGE,"E321"),sQuery(id+"F0.wireOp",EDGE,"E322"),sQuery(id+"F0.wireOp",EDGE,"E323"),sQuery(id+"F0.wireOp",EDGE,"E324"),sQuery(id+"F0.wireOp",EDGE,"E325"),sQuery(id+"F0.wireOp",EDGE,"E326"),sQuery(id+"F0.wireOp",EDGE,"E327"),sQuery(id+"F0.wireOp",EDGE,"E328"),sQuery(id+"F0.wireOp",EDGE,"E329"),sQuery(id+"F0.wireOp",EDGE,"E339"),sQuery(id+"F0.wireOp",EDGE,"E340"),sQuery(id+"F0.wireOp",EDGE,"E341"),sQuery(id+"F0.wireOp",EDGE,"E342"),sQuery(id+"F0.wireOp",EDGE,"E343"),sQuery(id+"F0.wireOp",EDGE,"E344"),sQuery(id+"F0.wireOp",EDGE,"E345"),sQuery(id+"F0.wireOp",EDGE,"E346"),sQuery(id+"F0.wireOp",EDGE,"E347"),sQuery(id+"F0.wireOp",EDGE,"E348"),sQuery(id+"F0.wireOp",EDGE,"E349"),sQuery(id+"F0.wireOp",EDGE,"E350"),sQuery(id+"F0.wireOp",EDGE,"E351"),sQuery(id+"F0.wireOp",EDGE,"E352"),sQuery(id+"F0.wireOp",EDGE,"E353"),sQuery(id+"F0.wireOp",EDGE,"E354"),sQuery(id+"F0.wireOp",EDGE,"E355"),sQuery(id+"F0.wireOp",EDGE,"E356"),sQuery(id+"F0.wireOp",EDGE,"E357"),sQuery(id+"F0.wireOp",EDGE,"E358"),sQuery(id+"F0.wireOp",EDGE,"E359"),sQuery(id+"F0.wireOp",EDGE,"E360"),sQuery(id+"F0.wireOp",EDGE,"E361"),sQuery(id+"F0.wireOp",EDGE,"E362"),sQuery(id+"F0.wireOp",EDGE,"E363"),sQuery(id+"F0.wireOp",EDGE,"E364"),sQuery(id+"F0.wireOp",EDGE,"E365"),sQuery(id+"F0.wireOp",EDGE,"E366"),sQuery(id+"F0.wireOp",EDGE,"E367"),sQuery(id+"F0.wireOp",EDGE,"E368"),sQuery(id+"F0.wireOp",EDGE,"E369"),sQuery(id+"F0.wireOp",EDGE,"E370"),sQuery(id+"F0.wireOp",EDGE,"E371"),sQuery(id+"F0.wireOp",EDGE,"E372"),sQuery(id+"F0.wireOp",EDGE,"E373"),sQuery(id+"F0.wireOp",EDGE,"E374"),sQuery(id+"F0.wireOp",EDGE,"E375"),sQuery(id+"F0.wireOp",EDGE,"E376"),sQuery(id+"F0.wireOp",EDGE,"E377"),sQuery(id+"F0.wireOp",EDGE,"E378"),sQuery(id+"F0.wireOp",EDGE,"E379"),sQuery(id+"F0.wireOp",EDGE,"E380"),sQuery(id+"F0.wireOp",EDGE,"E381"),sQuery(id+"F0.wireOp",EDGE,"E382"),sQuery(id+"F0.wireOp",EDGE,"E383"),sQuery(id+"F0.wireOp",EDGE,"E384"),sQuery(id+"F0.wireOp",EDGE,"E385"),sQuery(id+"F0.wireOp",EDGE,"E386"),sQuery(id+"F0.wireOp",EDGE,"E387"),sQuery(id+"F0.wireOp",EDGE,"E388"),sQuery(id+"F0.wireOp",EDGE,"E389"),sQuery(id+"F0.wireOp",EDGE,"E390"),sQuery(id+"F0.wireOp",EDGE,"E391"),sQuery(id+"F0.wireOp",EDGE,"E392"),sQuery(id+"F0.wireOp",EDGE,"E393"),sQuery(id+"F0.wireOp",EDGE,"E394"),sQuery(id+"F0.wireOp",EDGE,"E395"),sQuery(id+"F0.wireOp",EDGE,"E396"),sQuery(id+"F0.wireOp",EDGE,"E397"),sQuery(id+"F0.wireOp",EDGE,"E398")])],"isStart":false});
            var sketch = newSketch(context, id + "F3", { "sketchPlane" : qUnion([Q0])});
            skCircle(sketch, "E399", {"center": v(-9.94, 30.51) * mm, "radius": 2.2 * mm});
            skCircle(sketch, "E400", {"center": v(30.06, -9.49) * mm, "radius": 2.2 * mm});
            skSolve(sketch);
        }
        {
            var Q0;
            Q0=qSketchRegion(id+"F3",true);
            extrude(context, id + "F4", {"entities" : qUnion([Q0]), "operationType" : NewBodyOperationType.REMOVE, "oppositeDirection" : true, "depth" : 25 * mm});
        }
        {
            var Q0;
            Q0=makeQuery(id+"F0.imprint","IMPRINT",FACE,{"disambiguationData":[TD([[makeQuery(id+"F0.imprint","IMPRINT",EDGE,{"derivedFrom":sQuery(id+"F0.wireOp",EDGE,"E0")}),-1.0]])]});
            extrude(context, id + "F5", {"entities" : qUnion([Q0]), "oppositeDirection" : true, "depth" : 2 * mm});
        }
        {
            var Q0;
            Q0=makeQuery(id+"F5.opExtrude","CAP_FACE",FACE,{"disambiguationData":[OSD([sQuery(id+"F0.wireOp",EDGE,"E0"),sQuery(id+"F0.wireOp",EDGE,"E1"),sQuery(id+"F0.wireOp",EDGE,"E2"),sQuery(id+"F0.wireOp",EDGE,"E3"),sQuery(id+"F0.wireOp",EDGE,"E4"),sQuery(id+"F0.wireOp",EDGE,"E5"),sQuery(id+"F0.wireOp",EDGE,"E6"),sQuery(id+"F0.wireOp",EDGE,"E7"),sQuery(id+"F0.wireOp",EDGE,"E8"),sQuery(id+"F0.wireOp",EDGE,"E9"),sQuery(id+"F0.wireOp",EDGE,"E10"),sQuery(id+"F0.wireOp",EDGE,"E11"),sQuery(id+"F0.wireOp",EDGE,"E12"),sQuery(id+"F0.wireOp",EDGE,"E13"),sQuery(id+"F0.wireOp",EDGE,"E14"),sQuery(id+"F0.wireOp",EDGE,"E15"),sQuery(id+"F0.wireOp",EDGE,"E16"),sQuery(id+"F0.wireOp",EDGE,"E17"),sQuery(id+"F0.wireOp",EDGE,"E18"),sQuery(id+"F0.wireOp",EDGE,"E19"),sQuery(id+"F0.wireOp",EDGE,"E20"),sQuery(id+"F0.wireOp",EDGE,"E21"),sQuery(id+"F0.wireOp",EDGE,"E22"),sQuery(id+"F0.wireOp",EDGE,"E23"),sQuery(id+"F0.wireOp",EDGE,"E24"),sQuery(id+"F0.wireOp",EDGE,"E25"),sQuery(id+"F0.wireOp",EDGE,"E26"),sQuery(id+"F0.wireOp",EDGE,"E27"),sQuery(id+"F0.wireOp",EDGE,"E28"),sQuery(id+"F0.wireOp",EDGE,"E29"),sQuery(id+"F0.wireOp",EDGE,"E30"),sQuery(id+"F0.wireOp",EDGE,"E31"),sQuery(id+"F0.wireOp",EDGE,"E32"),sQuery(id+"F0.wireOp",EDGE,"E33"),sQuery(id+"F0.wireOp",EDGE,"E34"),sQuery(id+"F0.wireOp",EDGE,"E35"),sQuery(id+"F0.wireOp",EDGE,"E36"),sQuery(id+"F0.wireOp",EDGE,"E37"),sQuery(id+"F0.wireOp",EDGE,"E38"),sQuery(id+"F0.wireOp",EDGE,"E39"),sQuery(id+"F0.wireOp",EDGE,"E40"),sQuery(id+"F0.wireOp",EDGE,"E41"),sQuery(id+"F0.wireOp",EDGE,"E42"),sQuery(id+"F0.wireOp",EDGE,"E43"),sQuery(id+"F0.wireOp",EDGE,"E44"),sQuery(id+"F0.wireOp",EDGE,"E45"),sQuery(id+"F0.wireOp",EDGE,"E46"),sQuery(id+"F0.wireOp",EDGE,"E47"),sQuery(id+"F0.wireOp",EDGE,"E48"),sQuery(id+"F0.wireOp",EDGE,"E49"),sQuery(id+"F0.wireOp",EDGE,"E50"),sQuery(id+"F0.wireOp",EDGE,"E51"),sQuery(id+"F0.wireOp",EDGE,"E52"),sQuery(id+"F0.wireOp",EDGE,"E53"),sQuery(id+"F0.wireOp",EDGE,"E54"),sQuery(id+"F0.wireOp",EDGE,"E55"),sQuery(id+"F0.wireOp",EDGE,"E56"),sQuery(id+"F0.wireOp",EDGE,"E57"),sQuery(id+"F0.wireOp",EDGE,"E58"),sQuery(id+"F0.wireOp",EDGE,"E59"),sQuery(id+"F0.wireOp",EDGE,"E60"),sQuery(id+"F0.wireOp",EDGE,"E61"),sQuery(id+"F0.wireOp",EDGE,"E62"),sQuery(id+"F0.wireOp",EDGE,"E63"),sQuery(id+"F0.wireOp",EDGE,"E64"),sQuery(id+"F0.wireOp",EDGE,"E65"),sQuery(id+"F0.wireOp",EDGE,"E66"),sQuery(id+"F0.wireOp",EDGE,"E67"),sQuery(id+"F0.wireOp",EDGE,"E68"),sQuery(id+"F0.wireOp",EDGE,"E69"),sQuery(id+"F0.wireOp",EDGE,"E70"),sQuery(id+"F0.wireOp",EDGE,"E71"),sQuery(id+"F0.wireOp",EDGE,"E72"),sQuery(id+"F0.wireOp",EDGE,"E73"),sQuery(id+"F0.wireOp",EDGE,"E74"),sQuery(id+"F0.wireOp",EDGE,"E75"),sQuery(id+"F0.wireOp",EDGE,"E76"),sQuery(id+"F0.wireOp",EDGE,"E77"),sQuery(id+"F0.wireOp",EDGE,"E78"),sQuery(id+"F0.wireOp",EDGE,"E79"),sQuery(id+"F0.wireOp",EDGE,"E80"),sQuery(id+"F0.wireOp",EDGE,"E81"),sQuery(id+"F0.wireOp",EDGE,"E82"),sQuery(id+"F0.wireOp",EDGE,"E83"),sQuery(id+"F0.wireOp",EDGE,"E84"),sQuery(id+"F0.wireOp",EDGE,"E85"),sQuery(id+"F0.wireOp",EDGE,"E86"),sQuery(id+"F0.wireOp",EDGE,"E87"),sQuery(id+"F0.wireOp",EDGE,"E88"),sQuery(id+"F0.wireOp",EDGE,"E89"),sQuery(id+"F0.wireOp",EDGE,"E90"),sQuery(id+"F0.wireOp",EDGE,"E91"),sQuery(id+"F0.wireOp",EDGE,"E92"),sQuery(id+"F0.wireOp",EDGE,"E93"),sQuery(id+"F0.wireOp",EDGE,"E94"),sQuery(id+"F0.wireOp",EDGE,"E95"),sQuery(id+"F0.wireOp",EDGE,"E96"),sQuery(id+"F0.wireOp",EDGE,"E97"),sQuery(id+"F0.wireOp",EDGE,"E98"),sQuery(id+"F0.wireOp",EDGE,"E99"),sQuery(id+"F0.wireOp",EDGE,"E100"),sQuery(id+"F0.wireOp",EDGE,"E101"),sQuery(id+"F0.wireOp",EDGE,"E102"),sQuery(id+"F0.wireOp",EDGE,"E103"),sQuery(id+"F0.wireOp",EDGE,"E104"),sQuery(id+"F0.wireOp",EDGE,"E105"),sQuery(id+"F0.wireOp",EDGE,"E106"),sQuery(id+"F0.wireOp",EDGE,"E107"),sQuery(id+"F0.wireOp",EDGE,"E108"),sQuery(id+"F0.wireOp",EDGE,"E109"),sQuery(id+"F0.wireOp",EDGE,"E110"),sQuery(id+"F0.wireOp",EDGE,"E111"),sQuery(id+"F0.wireOp",EDGE,"E112"),sQuery(id+"F0.wireOp",EDGE,"E113"),sQuery(id+"F0.wireOp",EDGE,"E114"),sQuery(id+"F0.wireOp",EDGE,"E115"),sQuery(id+"F0.wireOp",EDGE,"E116"),sQuery(id+"F0.wireOp",EDGE,"E117"),sQuery(id+"F0.wireOp",EDGE,"E118"),sQuery(id+"F0.wireOp",EDGE,"E119"),sQuery(id+"F0.wireOp",EDGE,"E120"),sQuery(id+"F0.wireOp",EDGE,"E121"),sQuery(id+"F0.wireOp",EDGE,"E122"),sQuery(id+"F0.wireOp",EDGE,"E123"),sQuery(id+"F0.wireOp",EDGE,"E124"),sQuery(id+"F0.wireOp",EDGE,"E125"),sQuery(id+"F0.wireOp",EDGE,"E126"),sQuery(id+"F0.wireOp",EDGE,"E127"),sQuery(id+"F0.wireOp",EDGE,"E128"),sQuery(id+"F0.wireOp",EDGE,"E129"),sQuery(id+"F0.wireOp",EDGE,"E130"),sQuery(id+"F0.wireOp",EDGE,"E131"),sQuery(id+"F0.wireOp",EDGE,"E132"),sQuery(id+"F0.wireOp",EDGE,"E133"),sQuery(id+"F0.wireOp",EDGE,"E143"),sQuery(id+"F0.wireOp",EDGE,"E144"),sQuery(id+"F0.wireOp",EDGE,"E145"),sQuery(id+"F0.wireOp",EDGE,"E146"),sQuery(id+"F0.wireOp",EDGE,"E147"),sQuery(id+"F0.wireOp",EDGE,"E148"),sQuery(id+"F0.wireOp",EDGE,"E149"),sQuery(id+"F0.wireOp",EDGE,"E150"),sQuery(id+"F0.wireOp",EDGE,"E151"),sQuery(id+"F0.wireOp",EDGE,"E152"),sQuery(id+"F0.wireOp",EDGE,"E153"),sQuery(id+"F0.wireOp",EDGE,"E154"),sQuery(id+"F0.wireOp",EDGE,"E155"),sQuery(id+"F0.wireOp",EDGE,"E156"),sQuery(id+"F0.wireOp",EDGE,"E157"),sQuery(id+"F0.wireOp",EDGE,"E158"),sQuery(id+"F0.wireOp",EDGE,"E159"),sQuery(id+"F0.wireOp",EDGE,"E160"),sQuery(id+"F0.wireOp",EDGE,"E161"),sQuery(id+"F0.wireOp",EDGE,"E162"),sQuery(id+"F0.wireOp",EDGE,"E163"),sQuery(id+"F0.wireOp",EDGE,"E164"),sQuery(id+"F0.wireOp",EDGE,"E165"),sQuery(id+"F0.wireOp",EDGE,"E166"),sQuery(id+"F0.wireOp",EDGE,"E167"),sQuery(id+"F0.wireOp",EDGE,"E168"),sQuery(id+"F0.wireOp",EDGE,"E169"),sQuery(id+"F0.wireOp",EDGE,"E170"),sQuery(id+"F0.wireOp",EDGE,"E171"),sQuery(id+"F0.wireOp",EDGE,"E172"),sQuery(id+"F0.wireOp",EDGE,"E173"),sQuery(id+"F0.wireOp",EDGE,"E174"),sQuery(id+"F0.wireOp",EDGE,"E175"),sQuery(id+"F0.wireOp",EDGE,"E176"),sQuery(id+"F0.wireOp",EDGE,"E177"),sQuery(id+"F0.wireOp",EDGE,"E178"),sQuery(id+"F0.wireOp",EDGE,"E179"),sQuery(id+"F0.wireOp",EDGE,"E180"),sQuery(id+"F0.wireOp",EDGE,"E181"),sQuery(id+"F0.wireOp",EDGE,"E182"),sQuery(id+"F0.wireOp",EDGE,"E183"),sQuery(id+"F0.wireOp",EDGE,"E184"),sQuery(id+"F0.wireOp",EDGE,"E185"),sQuery(id+"F0.wireOp",EDGE,"E186"),sQuery(id+"F0.wireOp",EDGE,"E187"),sQuery(id+"F0.wireOp",EDGE,"E188"),sQuery(id+"F0.wireOp",EDGE,"E189"),sQuery(id+"F0.wireOp",EDGE,"E190"),sQuery(id+"F0.wireOp",EDGE,"E191"),sQuery(id+"F0.wireOp",EDGE,"E192"),sQuery(id+"F0.wireOp",EDGE,"E193"),sQuery(id+"F0.wireOp",EDGE,"E194"),sQuery(id+"F0.wireOp",EDGE,"E195"),sQuery(id+"F0.wireOp",EDGE,"E196"),sQuery(id+"F0.wireOp",EDGE,"E197"),sQuery(id+"F0.wireOp",EDGE,"E198"),sQuery(id+"F0.wireOp",EDGE,"E199"),sQuery(id+"F0.wireOp",EDGE,"E200"),sQuery(id+"F0.wireOp",EDGE,"E201"),sQuery(id+"F0.wireOp",EDGE,"E202"),sQuery(id+"F0.wireOp",EDGE,"E203"),sQuery(id+"F0.wireOp",EDGE,"E204"),sQuery(id+"F0.wireOp",EDGE,"E205"),sQuery(id+"F0.wireOp",EDGE,"E206"),sQuery(id+"F0.wireOp",EDGE,"E207"),sQuery(id+"F0.wireOp",EDGE,"E208"),sQuery(id+"F0.wireOp",EDGE,"E209"),sQuery(id+"F0.wireOp",EDGE,"E210"),sQuery(id+"F0.wireOp",EDGE,"E211"),sQuery(id+"F0.wireOp",EDGE,"E212"),sQuery(id+"F0.wireOp",EDGE,"E213"),sQuery(id+"F0.wireOp",EDGE,"E214"),sQuery(id+"F0.wireOp",EDGE,"E215"),sQuery(id+"F0.wireOp",EDGE,"E216"),sQuery(id+"F0.wireOp",EDGE,"E217"),sQuery(id+"F0.wireOp",EDGE,"E218"),sQuery(id+"F0.wireOp",EDGE,"E219"),sQuery(id+"F0.wireOp",EDGE,"E220"),sQuery(id+"F0.wireOp",EDGE,"E221"),sQuery(id+"F0.wireOp",EDGE,"E222"),sQuery(id+"F0.wireOp",EDGE,"E223"),sQuery(id+"F0.wireOp",EDGE,"E224"),sQuery(id+"F0.wireOp",EDGE,"E225"),sQuery(id+"F0.wireOp",EDGE,"E226"),sQuery(id+"F0.wireOp",EDGE,"E227"),sQuery(id+"F0.wireOp",EDGE,"E228"),sQuery(id+"F0.wireOp",EDGE,"E229"),sQuery(id+"F0.wireOp",EDGE,"E230"),sQuery(id+"F0.wireOp",EDGE,"E231"),sQuery(id+"F0.wireOp",EDGE,"E232"),sQuery(id+"F0.wireOp",EDGE,"E233"),sQuery(id+"F0.wireOp",EDGE,"E234"),sQuery(id+"F0.wireOp",EDGE,"E235"),sQuery(id+"F0.wireOp",EDGE,"E236"),sQuery(id+"F0.wireOp",EDGE,"E237"),sQuery(id+"F0.wireOp",EDGE,"E238"),sQuery(id+"F0.wireOp",EDGE,"E239"),sQuery(id+"F0.wireOp",EDGE,"E240"),sQuery(id+"F0.wireOp",EDGE,"E241"),sQuery(id+"F0.wireOp",EDGE,"E242"),sQuery(id+"F0.wireOp",EDGE,"E243"),sQuery(id+"F0.wireOp",EDGE,"E244"),sQuery(id+"F0.wireOp",EDGE,"E245"),sQuery(id+"F0.wireOp",EDGE,"E246"),sQuery(id+"F0.wireOp",EDGE,"E247"),sQuery(id+"F0.wireOp",EDGE,"E248"),sQuery(id+"F0.wireOp",EDGE,"E249"),sQuery(id+"F0.wireOp",EDGE,"E250"),sQuery(id+"F0.wireOp",EDGE,"E251"),sQuery(id+"F0.wireOp",EDGE,"E252"),sQuery(id+"F0.wireOp",EDGE,"E253"),sQuery(id+"F0.wireOp",EDGE,"E254"),sQuery(id+"F0.wireOp",EDGE,"E255"),sQuery(id+"F0.wireOp",EDGE,"E256"),sQuery(id+"F0.wireOp",EDGE,"E257"),sQuery(id+"F0.wireOp",EDGE,"E258"),sQuery(id+"F0.wireOp",EDGE,"E259"),sQuery(id+"F0.wireOp",EDGE,"E260"),sQuery(id+"F0.wireOp",EDGE,"E261"),sQuery(id+"F0.wireOp",EDGE,"E262"),sQuery(id+"F0.wireOp",EDGE,"E263"),sQuery(id+"F0.wireOp",EDGE,"E264"),sQuery(id+"F0.wireOp",EDGE,"E265"),sQuery(id+"F0.wireOp",EDGE,"E266"),sQuery(id+"F0.wireOp",EDGE,"E267"),sQuery(id+"F0.wireOp",EDGE,"E268"),sQuery(id+"F0.wireOp",EDGE,"E269"),sQuery(id+"F0.wireOp",EDGE,"E270"),sQuery(id+"F0.wireOp",EDGE,"E271"),sQuery(id+"F0.wireOp",EDGE,"E272"),sQuery(id+"F0.wireOp",EDGE,"E273"),sQuery(id+"F0.wireOp",EDGE,"E274"),sQuery(id+"F0.wireOp",EDGE,"E275"),sQuery(id+"F0.wireOp",EDGE,"E276"),sQuery(id+"F0.wireOp",EDGE,"E277"),sQuery(id+"F0.wireOp",EDGE,"E278"),sQuery(id+"F0.wireOp",EDGE,"E286"),sQuery(id+"F0.wireOp",EDGE,"E287"),sQuery(id+"F0.wireOp",EDGE,"E288"),sQuery(id+"F0.wireOp",EDGE,"E289"),sQuery(id+"F0.wireOp",EDGE,"E290"),sQuery(id+"F0.wireOp",EDGE,"E291"),sQuery(id+"F0.wireOp",EDGE,"E292"),sQuery(id+"F0.wireOp",EDGE,"E293"),sQuery(id+"F0.wireOp",EDGE,"E294"),sQuery(id+"F0.wireOp",EDGE,"E295"),sQuery(id+"F0.wireOp",EDGE,"E296"),sQuery(id+"F0.wireOp",EDGE,"E297"),sQuery(id+"F0.wireOp",EDGE,"E298"),sQuery(id+"F0.wireOp",EDGE,"E299"),sQuery(id+"F0.wireOp",EDGE,"E300"),sQuery(id+"F0.wireOp",EDGE,"E301"),sQuery(id+"F0.wireOp",EDGE,"E302"),sQuery(id+"F0.wireOp",EDGE,"E303"),sQuery(id+"F0.wireOp",EDGE,"E304"),sQuery(id+"F0.wireOp",EDGE,"E305"),sQuery(id+"F0.wireOp",EDGE,"E306"),sQuery(id+"F0.wireOp",EDGE,"E307"),sQuery(id+"F0.wireOp",EDGE,"E308"),sQuery(id+"F0.wireOp",EDGE,"E309"),sQuery(id+"F0.wireOp",EDGE,"E310"),sQuery(id+"F0.wireOp",EDGE,"E311"),sQuery(id+"F0.wireOp",EDGE,"E312"),sQuery(id+"F0.wireOp",EDGE,"E313"),sQuery(id+"F0.wireOp",EDGE,"E314"),sQuery(id+"F0.wireOp",EDGE,"E315"),sQuery(id+"F0.wireOp",EDGE,"E316"),sQuery(id+"F0.wireOp",EDGE,"E317"),sQuery(id+"F0.wireOp",EDGE,"E318"),sQuery(id+"F0.wireOp",EDGE,"E319"),sQuery(id+"F0.wireOp",EDGE,"E320"),sQuery(id+"F0.wireOp",EDGE,"E321"),sQuery(id+"F0.wireOp",EDGE,"E322"),sQuery(id+"F0.wireOp",EDGE,"E323"),sQuery(id+"F0.wireOp",EDGE,"E324"),sQuery(id+"F0.wireOp",EDGE,"E325"),sQuery(id+"F0.wireOp",EDGE,"E326"),sQuery(id+"F0.wireOp",EDGE,"E327"),sQuery(id+"F0.wireOp",EDGE,"E328"),sQuery(id+"F0.wireOp",EDGE,"E329"),sQuery(id+"F0.wireOp",EDGE,"E339"),sQuery(id+"F0.wireOp",EDGE,"E340"),sQuery(id+"F0.wireOp",EDGE,"E341"),sQuery(id+"F0.wireOp",EDGE,"E342"),sQuery(id+"F0.wireOp",EDGE,"E343"),sQuery(id+"F0.wireOp",EDGE,"E344"),sQuery(id+"F0.wireOp",EDGE,"E345"),sQuery(id+"F0.wireOp",EDGE,"E346"),sQuery(id+"F0.wireOp",EDGE,"E347"),sQuery(id+"F0.wireOp",EDGE,"E348"),sQuery(id+"F0.wireOp",EDGE,"E349"),sQuery(id+"F0.wireOp",EDGE,"E350"),sQuery(id+"F0.wireOp",EDGE,"E351"),sQuery(id+"F0.wireOp",EDGE,"E352"),sQuery(id+"F0.wireOp",EDGE,"E353"),sQuery(id+"F0.wireOp",EDGE,"E354"),sQuery(id+"F0.wireOp",EDGE,"E355"),sQuery(id+"F0.wireOp",EDGE,"E356"),sQuery(id+"F0.wireOp",EDGE,"E357"),sQuery(id+"F0.wireOp",EDGE,"E358"),sQuery(id+"F0.wireOp",EDGE,"E359"),sQuery(id+"F0.wireOp",EDGE,"E360"),sQuery(id+"F0.wireOp",EDGE,"E361"),sQuery(id+"F0.wireOp",EDGE,"E362"),sQuery(id+"F0.wireOp",EDGE,"E363"),sQuery(id+"F0.wireOp",EDGE,"E364"),sQuery(id+"F0.wireOp",EDGE,"E365"),sQuery(id+"F0.wireOp",EDGE,"E366"),sQuery(id+"F0.wireOp",EDGE,"E367"),sQuery(id+"F0.wireOp",EDGE,"E368"),sQuery(id+"F0.wireOp",EDGE,"E369"),sQuery(id+"F0.wireOp",EDGE,"E370"),sQuery(id+"F0.wireOp",EDGE,"E371"),sQuery(id+"F0.wireOp",EDGE,"E372"),sQuery(id+"F0.wireOp",EDGE,"E373"),sQuery(id+"F0.wireOp",EDGE,"E374"),sQuery(id+"F0.wireOp",EDGE,"E375"),sQuery(id+"F0.wireOp",EDGE,"E376"),sQuery(id+"F0.wireOp",EDGE,"E377"),sQuery(id+"F0.wireOp",EDGE,"E378"),sQuery(id+"F0.wireOp",EDGE,"E379"),sQuery(id+"F0.wireOp",EDGE,"E380"),sQuery(id+"F0.wireOp",EDGE,"E381"),sQuery(id+"F0.wireOp",EDGE,"E382"),sQuery(id+"F0.wireOp",EDGE,"E383"),sQuery(id+"F0.wireOp",EDGE,"E384"),sQuery(id+"F0.wireOp",EDGE,"E385"),sQuery(id+"F0.wireOp",EDGE,"E386"),sQuery(id+"F0.wireOp",EDGE,"E387"),sQuery(id+"F0.wireOp",EDGE,"E388"),sQuery(id+"F0.wireOp",EDGE,"E389"),sQuery(id+"F0.wireOp",EDGE,"E390"),sQuery(id+"F0.wireOp",EDGE,"E391"),sQuery(id+"F0.wireOp",EDGE,"E392"),sQuery(id+"F0.wireOp",EDGE,"E393"),sQuery(id+"F0.wireOp",EDGE,"E394"),sQuery(id+"F0.wireOp",EDGE,"E395"),sQuery(id+"F0.wireOp",EDGE,"E396"),sQuery(id+"F0.wireOp",EDGE,"E397"),sQuery(id+"F0.wireOp",EDGE,"E398")])],"isStart":true});
            var sketch = newSketch(context, id + "F6", { "sketchPlane" : qUnion([Q0])});
            skCircle(sketch, "E401", {"center": v(-24.14, 36.5) * mm, "radius": 1.82 * mm});
            skCircle(sketch, "E402.1.0.0", {"center": v(-17.83, 36.5) * mm, "radius": 1.82 * mm});
            skCircle(sketch, "E402.2.0.0", {"center": v(-11.52, 36.5) * mm, "radius": 1.82 * mm});
            skCircle(sketch, "E402.3.0.0", {"center": v(-5.21, 36.5) * mm, "radius": 1.82 * mm});
            skCircle(sketch, "E402.4.0.0", {"center": v(1.1, 36.5) * mm, "radius": 1.82 * mm});
            skCircle(sketch, "E402.5.0.0", {"center": v(7.4, 36.5) * mm, "radius": 1.82 * mm});
            skCircle(sketch, "E402.6.0.0", {"center": v(13.71, 36.5) * mm, "radius": 1.82 * mm});
            skCircle(sketch, "E402.7.0.0", {"center": v(20.02, 36.5) * mm, "radius": 1.82 * mm});
            skCircle(sketch, "E402.8.0.0", {"center": v(26.33, 36.5) * mm, "radius": 1.82 * mm});
            skCircle(sketch, "E402.9.0.0", {"center": v(32.64, 36.5) * mm, "radius": 1.82 * mm});
            skLineSegment(sketch, "E402.direction1", {"start": v(-24.14, 36.5) * mm, "end": v(-17.83, 36.5) * mm, "construction": true});
            skCircle(sketch, "E403.1.0.0", {"center": v(32.63, 30.1) * mm, "radius": 1.82 * mm});
            skCircle(sketch, "E403.2.0.0", {"center": v(32.63, 23.7) * mm, "radius": 1.82 * mm});
            skCircle(sketch, "E403.3.0.0", {"center": v(32.62, 17.29) * mm, "radius": 1.82 * mm});
            skCircle(sketch, "E403.4.0.0", {"center": v(32.62, 10.88) * mm, "radius": 1.82 * mm});
            skCircle(sketch, "E403.5.0.0", {"center": v(32.61, 4.48) * mm, "radius": 1.82 * mm});
            skCircle(sketch, "E403.6.0.0", {"center": v(32.6, -1.93) * mm, "radius": 1.82 * mm});
            skCircle(sketch, "E403.7.0.0", {"center": v(32.6, -8.33) * mm, "radius": 1.82 * mm});
            skCircle(sketch, "E403.8.0.0", {"center": v(32.6, -14.74) * mm, "radius": 1.82 * mm});
            skCircle(sketch, "E403.9.0.0", {"center": v(32.6, -21.15) * mm, "radius": 1.82 * mm});
            skLineSegment(sketch, "E403.direction1", {"start": v(32.64, 36.5) * mm, "end": v(32.63, 30.1) * mm, "construction": true});
            skCircle(sketch, "E404.1.0.0", {"center": v(26.31, 30.02) * mm, "radius": 1.82 * mm});
            skCircle(sketch, "E404.2.0.0", {"center": v(26.3, 23.53) * mm, "radius": 1.82 * mm});
            skCircle(sketch, "E404.3.0.0", {"center": v(26.27, 17.04) * mm, "radius": 1.82 * mm});
            skCircle(sketch, "E404.4.0.0", {"center": v(26.25, 10.55) * mm, "radius": 1.82 * mm});
            skCircle(sketch, "E404.5.0.0", {"center": v(26.23, 4.06) * mm, "radius": 1.82 * mm});
            skCircle(sketch, "E404.6.0.0", {"center": v(26.2, -2.42) * mm, "radius": 1.82 * mm});
            skCircle(sketch, "E404.7.0.0", {"center": v(26.19, -8.91) * mm, "radius": 1.82 * mm});
            skCircle(sketch, "E404.8.0.0", {"center": v(26.17, -15.4) * mm, "radius": 1.82 * mm});
            skLineSegment(sketch, "E404.direction1", {"start": v(26.33, 36.5) * mm, "end": v(26.31, 30.02) * mm, "construction": true});
            skSolve(sketch);
        }
        {
            var Q0;
            Q0=qSketchRegion(id+"F6",true);
            extrude(context, id + "F7", {"entities" : qUnion([Q0]), "operationType" : NewBodyOperationType.REMOVE, "oppositeDirection" : true, "depth" : 5 * mm});
        }
    });
